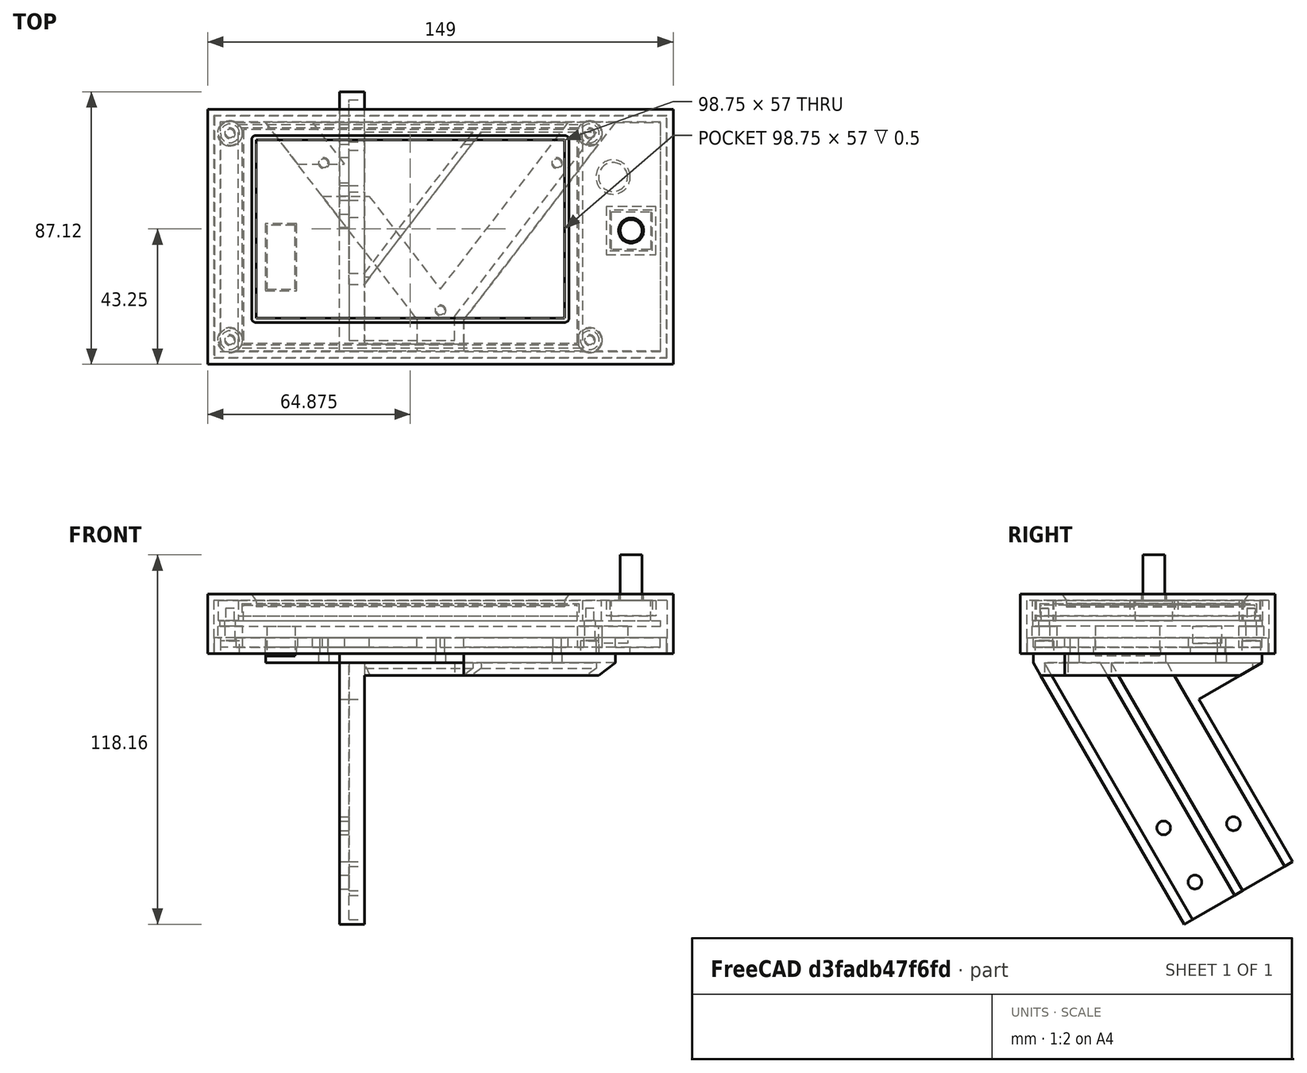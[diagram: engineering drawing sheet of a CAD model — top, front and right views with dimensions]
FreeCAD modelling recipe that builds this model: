
FCSTD DOCUMENT  (FreeCAD 0.20R24840 (Git))
Label: ender 3 v2 dwin case
License: Creative Commons Attribution
LicenseURL: http://creativecommons.org/licenses/by/4.0/
objects: Sketcher::SketchObject×41, PartDesign::Pad×23, PartDesign::Pocket×14, PartDesign::Body×5, PartDesign::SubShapeBinder×5, PartDesign::Groove×4, Part::Feature×2, Part::Mirroring×2, App::Part×1
note: 137 computed .brp shape members not serialized (recipe doc carries the construction recipe); baked Part::Feature solids carry a one-line shape summary decoded from their .brp

FEATURE [Sketcher::SketchObject] Sketch
  FullyConstrained = true
  MapMode = 5
  Support = -> [XY_Plane]
  sketch-geometry (4):
    g0: LineSegment StartX=0 StartY=0 StartZ=0 EndX=141 EndY=0 EndZ=0
    g1: LineSegment StartX=141 StartY=0 StartZ=0 EndX=141 EndY=73.5 EndZ=0
    g2: LineSegment StartX=141 StartY=73.5 StartZ=0 EndX=0 EndY=73.5 EndZ=0
    g3: LineSegment StartX=0 StartY=73.5 StartZ=0 EndX=0 EndY=0 EndZ=0
  constraints (11):
    c: Coincident(g0,g1)
    c: Coincident(g1,g2)
    c: Coincident(g2,g3)
    c: Coincident(g3,g0)
    c: Horizontal(g0)
    c: Horizontal(g2)
    c: Vertical(g1)
    c: Vertical(g3)
    c: Coincident(g0,g-1)
    c: Distance(g2) = 141
    c: Distance(g3) = 73.5
FEATURE [PartDesign::Pad] Pad
  Direction = (0,0,1)
  Length = 1.75
  Length2 = 100
  Profile = -> Sketch
  Type = 0
FEATURE [Sketcher::SketchObject] Sketch001
  FullyConstrained = true
  MapMode = 5
  Placement = pos=(0,0,1.75) rot=(0,0,1;0rad)
  Support = -> [Pad]
  sketch-geometry (4):
    g0: LineSegment StartX=7.5 StartY=2.75 StartZ=0 EndX=114.25 EndY=2.75 EndZ=0
    g1: LineSegment StartX=114.25 StartY=2.75 StartZ=0 EndX=114.25 EndY=71 EndZ=0
    g2: LineSegment StartX=114.25 StartY=71 StartZ=0 EndX=7.5 EndY=71 EndZ=0
    g3: LineSegment StartX=7.5 StartY=71 StartZ=0 EndX=7.5 EndY=2.75 EndZ=0
  constraints (12):
    c: Coincident(g0,g1)
    c: Coincident(g1,g2)
    c: Coincident(g2,g3)
    c: Coincident(g3,g0)
    c: Horizontal(g0)
    c: Horizontal(g2)
    c: Vertical(g1)
    c: Vertical(g3)
    c: Distance(g3) = 68.25
    c: Distance(g2) = 106.75
    c: DistanceX(g-1,g0) = 7.5
    c: DistanceY(g-1,g0) = 2.75
FEATURE [PartDesign::Pad] Pad001
  BaseFeature = -> Pad
  Direction = (0,0,1)
  Length = 5
  Length2 = 100
  Profile = -> Sketch001
  Type = 0
FEATURE [Sketcher::SketchObject] Sketch002
  ExternalGeometry = -> [Pad001]
  FullyConstrained = true
  MapMode = 5
  Placement = pos=(0,0,6.75) rot=(0,0,1;0rad)
  Support = -> [Pad001]
  sketch-geometry (8):
    g0: LineSegment StartX=11.5 StartY=67.75 StartZ=0 EndX=110.25 EndY=67.75 EndZ=0
    g1: LineSegment StartX=110.25 StartY=67.75 StartZ=0 EndX=110.25 EndY=10.75 EndZ=0
    g2: LineSegment StartX=110.25 StartY=10.75 StartZ=0 EndX=11.5 EndY=10.75 EndZ=0
    g3: LineSegment StartX=11.5 StartY=10.75 StartZ=0 EndX=11.5 EndY=67.75 EndZ=0
    g4: LineSegment StartX=110.25 StartY=67.75 StartZ=0 EndX=114.25 EndY=67.75 EndZ=0
    g5: LineSegment StartX=11.5 StartY=67.75 StartZ=0 EndX=7.5 EndY=67.75 EndZ=0
    g6: LineSegment StartX=11.5 StartY=67.75 StartZ=0 EndX=11.5 EndY=71 EndZ=0
    g7: LineSegment StartX=11.5 StartY=10.75 StartZ=0 EndX=11.5 EndY=2.75 EndZ=0
  constraints (24):
    c: Coincident(g0,g1)
    c: Coincident(g1,g2)
    c: Coincident(g2,g3)
    c: Coincident(g3,g0)
    c: Horizontal(g0)
    c: Horizontal(g2)
    c: Vertical(g1)
    c: Vertical(g3)
    c: Coincident(g4,g0)
    c: PointOnObject(g4,g-4)
    c: Coincident(g5,g0)
    c: PointOnObject(g5,g-6)
    c: Coincident(g6,g0)
    c: PointOnObject(g6,g-3)
    c: Vertical(g6)
    c: Coincident(g7,g2)
    c: PointOnObject(g7,g-5)
    c: Vertical(g7)
    c: Horizontal(g5)
    c: Horizontal(g4)
    c: Distance(g5) = 4
    c: Distance(g6) = 3.25
    c: Equal(g5,g4)
    c: Distance(g7) = 8
FEATURE [PartDesign::Pocket] Pocket
  BaseFeature = -> Pad001
  Length = 0.5
  Length2 = 100
  Profile = -> Sketch002
  Type = 0
FEATURE [Sketcher::SketchObject] Sketch003
  ExternalGeometry = -> [Pocket]
  FullyConstrained = true
  MapMode = 5
  Placement = pos=(0,0,1.75) rot=(0,0,1;0rad)
  Support = -> [Pocket]
  sketch-geometry (4):
    g0: LineSegment StartX=125.25 StartY=44.75 StartZ=0 EndX=137.75 EndY=44.75 EndZ=0
    g1: LineSegment StartX=137.75 StartY=44.75 StartZ=0 EndX=137.75 EndY=32.75 EndZ=0
    g2: LineSegment StartX=137.75 StartY=32.75 StartZ=0 EndX=125.25 EndY=32.75 EndZ=0
    g3: LineSegment StartX=125.25 StartY=32.75 StartZ=0 EndX=125.25 EndY=44.75 EndZ=0
  constraints (12):
    c: Coincident(g0,g1)
    c: Coincident(g1,g2)
    c: Coincident(g2,g3)
    c: Coincident(g3,g0)
    c: Horizontal(g0)
    c: Horizontal(g2)
    c: Vertical(g1)
    c: Vertical(g3)
    c: Distance(g0) = 12.5
    c: Distance(g1) = 12
    c: DistanceY(g0,g-3) = 28.75
    c: DistanceX(g0,g-3) = 3.25
FEATURE [PartDesign::Pad] Pad002
  BaseFeature = -> Pocket
  Direction = (0,0,1)
  Length = 6.35
  Length2 = 100
  Profile = -> Sketch003
  Type = 0
FEATURE [Sketcher::SketchObject] Sketch004
  ExternalGeometry = -> [Pad002]
  FullyConstrained = true
  MapMode = 5
  Placement = pos=(0,0,8.1) rot=(0,0,1;0rad)
  Support = -> [Pad002]
  sketch-geometry (5):
    g0: Circle CenterX=131.5 CenterY=38.75 CenterZ=0 NormalX=0 NormalY=0 NormalZ=1 AngleXU=0 Radius=3.5
    g1: LineSegment StartX=131.5 StartY=38.75 StartZ=0 EndX=131.5 EndY=44.75 EndZ=0
    g2: LineSegment StartX=131.5 StartY=38.75 StartZ=0 EndX=131.5 EndY=32.75 EndZ=0
    g3: LineSegment StartX=131.5 StartY=38.75 StartZ=0 EndX=137.75 EndY=38.75 EndZ=0
    g4: LineSegment StartX=131.5 StartY=38.75 StartZ=0 EndX=125.25 EndY=38.75 EndZ=0
  constraints (15):
    c: Radius(g0) = 3.5
    c: Coincident(g1,g0)
    c: PointOnObject(g1,g-3)
    c: Vertical(g1)
    c: Coincident(g2,g0)
    c: PointOnObject(g2,g-4)
    c: Vertical(g2)
    c: Coincident(g3,g0)
    c: PointOnObject(g3,g-6)
    c: Horizontal(g3)
    c: Coincident(g4,g0)
    c: PointOnObject(g4,g-5)
    c: Horizontal(g4)
    c: Equal(g3,g4)
    c: Equal(g1,g2)
FEATURE [PartDesign::Pad] Pad003
  BaseFeature = -> Pad002
  Direction = (0,0,1)
  Length = 14.75
  Length2 = 100
  Profile = -> Sketch004
  Type = 0
FEATURE [Sketcher::SketchObject] Sketch005
  ExternalGeometry = -> [Pad003]
  FullyConstrained = true
  MapMode = 5
  Placement = pos=(0,0,0) rot=(1,0,0;3.14159rad)
  Support = -> [Pad003]
  sketch-geometry (5):
    g0: Circle CenterX=125.725 CenterY=-55.875 CenterZ=0 NormalX=0 NormalY=0 NormalZ=1 AngleXU=0 Radius=4.625
    g1: LineSegment StartX=130.35 StartY=-55.875 StartZ=0 EndX=141 EndY=-55.875 EndZ=0
    g2: LineSegment StartX=130.35 StartY=-55.875 StartZ=0 EndX=125.725 EndY=-55.875 EndZ=0
    g3: LineSegment StartX=125.725 StartY=-60.5 StartZ=0 EndX=125.725 EndY=-73.5 EndZ=0
    g4: LineSegment StartX=125.725 StartY=-60.5 StartZ=0 EndX=125.725 EndY=-55.875 EndZ=0
  constraints (15):
    c: Radius(g0) = 4.625
    c: PointOnObject(g1,g0)
    c: PointOnObject(g1,g-3)
    c: Horizontal(g1)
    c: Distance(g1) = 10.65
    c: Coincident(g2,g1)
    c: Coincident(g2,g0)
    c: Horizontal(g2)
    c: PointOnObject(g3,g0)
    c: PointOnObject(g3,g-4)
    c: Vertical(g3)
    c: Coincident(g4,g3)
    c: Coincident(g4,g0)
    c: Vertical(g4)
    c: Distance(g3) = 13
FEATURE [PartDesign::Pad] Pad004
  BaseFeature = -> Pad003
  Direction = (0,0,-1)
  Length = 5.5
  Length2 = 100
  Profile = -> Sketch005
  Type = 0
FEATURE [Sketcher::SketchObject] Sketch006
  FullyConstrained = true
  MapMode = 5
  Placement = pos=(0,0,0) rot=(1,0,0;3.14159rad)
  Support = -> [Pad004]
  sketch-geometry (4):
    g0: LineSegment StartX=15 StartY=-20 StartZ=0 EndX=24 EndY=-20 EndZ=0
    g1: LineSegment StartX=24 StartY=-20 StartZ=0 EndX=24 EndY=-40.5 EndZ=0
    g2: LineSegment StartX=24 StartY=-40.5 StartZ=0 EndX=15 EndY=-40.5 EndZ=0
    g3: LineSegment StartX=15 StartY=-40.5 StartZ=0 EndX=15 EndY=-20 EndZ=0
  constraints (12):
    c: Coincident(g0,g1)
    c: Coincident(g1,g2)
    c: Coincident(g2,g3)
    c: Coincident(g3,g0)
    c: Horizontal(g0)
    c: Horizontal(g2)
    c: Vertical(g1)
    c: Vertical(g3)
    c: Distance(g2) = 9
    c: Distance(g3) = 20.5
    c: DistanceY(g0,g-1) = 20
    c: DistanceX(g-1,g0) = 15
FEATURE [PartDesign::Pad] Pad005
  BaseFeature = -> Pad004
  Direction = (0,0,-1)
  Length = 9.5
  Length2 = 100
  Profile = -> Sketch006
  Type = 0
FEATURE [Sketcher::SketchObject] Sketch007
  ExternalGeometry = -> [Pad005]
  FullyConstrained = true
  MapMode = 5
  Placement = pos=(0,0,1.75) rot=(0,0,1;0rad)
  Support = -> [Pad005]
  sketch-geometry (19):
    g0: Circle CenterX=3.1665 CenterY=3.6665 CenterZ=0 NormalX=0 NormalY=0 NormalZ=1 AngleXU=0 Radius=1.6665
    g1: Circle CenterX=3.1665 CenterY=69.8335 CenterZ=0 NormalX=0 NormalY=0 NormalZ=1 AngleXU=0 Radius=1.6665
    g2: LineSegment StartX=3.1665 StartY=71.5 StartZ=0 EndX=3.1665 EndY=73.5 EndZ=0
    g3: LineSegment StartX=3.1665 StartY=69.8335 StartZ=0 EndX=3.1665 EndY=71.5 EndZ=0
    g4: LineSegment StartX=3.1665 StartY=69.8335 StartZ=0 EndX=1.5 EndY=69.8335 EndZ=0
    g5: LineSegment StartX=1.5 StartY=69.8335 StartZ=0 EndX=0 EndY=69.8335 EndZ=0
    g6: LineSegment StartX=3.1665 StartY=3.6665 StartZ=0 EndX=3.1665 EndY=2 EndZ=0
    g7: LineSegment StartX=3.1665 StartY=3.6665 StartZ=0 EndX=1.5 EndY=3.6665 EndZ=0
    g8: LineSegment StartX=1.5 StartY=3.6665 StartZ=0 EndX=0 EndY=3.6665 EndZ=0
    g9: LineSegment StartX=3.1665 StartY=2 StartZ=0 EndX=3.1665 EndY=0 EndZ=0
    g10: Circle CenterX=118.284 CenterY=3.6665 CenterZ=0 NormalX=0 NormalY=0 NormalZ=1 AngleXU=0 Radius=1.6665
    g11: Circle CenterX=118.284 CenterY=69.8335 CenterZ=0 NormalX=0 NormalY=0 NormalZ=1 AngleXU=0 Radius=1.6665
    g12: LineSegment StartX=118.284 StartY=3.6665 StartZ=0 EndX=118.284 EndY=2 EndZ=0
    g13: LineSegment StartX=118.284 StartY=2 StartZ=0 EndX=118.284 EndY=0 EndZ=0
    g14: LineSegment StartX=118.284 StartY=69.8335 StartZ=0 EndX=118.284 EndY=71.5 EndZ=0
    g15: LineSegment StartX=118.284 StartY=71.5 StartZ=0 EndX=118.284 EndY=73.5 EndZ=0
    g16: LineSegment StartX=118.284 StartY=69.8335 StartZ=0 EndX=118.284 EndY=3.6665 EndZ=0
    g17: LineSegment StartX=141 StartY=3.6665 StartZ=0 EndX=119.95 EndY=3.6665 EndZ=0
    g18: LineSegment StartX=119.95 StartY=3.6665 StartZ=0 EndX=118.284 EndY=3.6665 EndZ=0
  constraints (56):
    c: Radius(g0) = 1.6665
    c: Equal(g1,g0)
    c: PointOnObject(g2,g1)
    c: PointOnObject(g2,g-6)
    c: Vertical(g2)
    c: Coincident(g3,g1)
    c: Coincident(g3,g2)
    c: Vertical(g3)
    c: Coincident(g4,g1)
    c: PointOnObject(g4,g1)
    c: Horizontal(g4)
    c: Coincident(g5,g4)
    c: PointOnObject(g5,g-4)
    c: Horizontal(g5)
    c: Distance(g2) = 2
    c: Distance(g5) = 1.5
    c: Coincident(g6,g0)
    c: PointOnObject(g6,g0)
    c: Vertical(g6)
    c: Coincident(g7,g0)
    c: PointOnObject(g7,g0)
    c: Horizontal(g7)
    c: Coincident(g8,g7)
    c: PointOnObject(g8,g-4)
    c: Horizontal(g8)
    c: Coincident(g9,g6)
    c: PointOnObject(g9,g-3)
    c: Vertical(g9)
    c: Distance(g8) = 1.5
    c: Distance(g9) = 2
    c: Equal(g10,g11)
    c: Equal(g11,g1)
    c: Coincident(g12,g10)
    c: PointOnObject(g12,g10)
    c: Vertical(g12)
    c: Coincident(g13,g12)
    c: PointOnObject(g13,g-3)
    c: Vertical(g13)
    c: Distance(g13) = 2
    c: Coincident(g14,g11)
    c: PointOnObject(g14,g11)
    c: Vertical(g14)
    c: Coincident(g15,g14)
    c: PointOnObject(g15,g-6)
    c: Vertical(g15)
    c: Distance(g15) = 2
    c: Coincident(g16,g11)
    c: Coincident(g16,g10)
    c: Vertical(g16)
    c: PointOnObject(g17,g-5)
    c: PointOnObject(g17,g10)
    c: Horizontal(g17)
    c: Coincident(g18,g17)
    c: Coincident(g18,g10)
    c: Horizontal(g18)
    c: Distance(g17) = 21.05
FEATURE [PartDesign::Pocket] Pocket001
  BaseFeature = -> Pad005
  Length = 5
  Length2 = 100
  Profile = -> Sketch007
  Type = 1
FEATURE [PartDesign::Body] Body  label="T5UIC1"
  Group = -> [Sketch,Pad,Sketch001,Pad001,Sketch002,Pocket,Sketch003,Pad002,Sketch004,Pad003,Sketch005,Pad004,Sketch006,Pad005,Sketch007,Pocket001]
  Origin = -> Origin
  Tip = -> Pocket001
FEATURE [PartDesign::SubShapeBinder] Binder
  BindMode = 0
  ClaimChildren = false
  Context = -> Body001 [Binder.]
  Fuse = false
  MakeFace = true
  PartialLoad = false
  Relative = true
  Support = -> [Body]
  _Version = 2
FEATURE [Sketcher::SketchObject] Sketch008
  AttachmentOffset = pos=(0,0,0.2) rot=(0,0,1;0rad)
  ExternalGeometry = -> [Binder]
  FullyConstrained = true
  MapMode = 5
  Placement = pos=(0,0,8.3) rot=(0,0,1;0rad)
  Support = -> [Binder]
  sketch-geometry (9):
    g0: LineSegment StartX=-4 StartY=77.5 StartZ=0 EndX=145 EndY=77.5 EndZ=0
    g1: LineSegment StartX=145 StartY=77.5 StartZ=0 EndX=145 EndY=-4 EndZ=0
    g2: LineSegment StartX=145 StartY=-4 StartZ=0 EndX=-4 EndY=-4 EndZ=0
    g3: LineSegment StartX=-4 StartY=-4 StartZ=0 EndX=-4 EndY=77.5 EndZ=0
    g4: LineSegment StartX=11.5 StartY=67.75 StartZ=0 EndX=110.25 EndY=67.75 EndZ=0
    g5: LineSegment StartX=110.25 StartY=67.75 StartZ=0 EndX=110.25 EndY=10.75 EndZ=0
    g6: LineSegment StartX=110.25 StartY=10.75 StartZ=0 EndX=11.5 EndY=10.75 EndZ=0
    g7: LineSegment StartX=11.5 StartY=10.75 StartZ=0 EndX=11.5 EndY=67.75 EndZ=0
    g8: Circle CenterX=131.5 CenterY=38.75 CenterZ=0 NormalX=0 NormalY=0 NormalZ=1 AngleXU=0 Radius=4
  constraints (24):
    c: Coincident(g0,g1)
    c: Coincident(g1,g2)
    c: Coincident(g2,g3)
    c: Coincident(g3,g0)
    c: Horizontal(g0)
    c: Horizontal(g2)
    c: Vertical(g1)
    c: Vertical(g3)
    c: Coincident(g4,g5)
    c: Coincident(g5,g6)
    c: Coincident(g6,g7)
    c: Coincident(g7,g4)
    c: Horizontal(g4)
    c: Horizontal(g6)
    c: Vertical(g5)
    c: Vertical(g7)
    c: Coincident(g4,g-6)
    c: Coincident(g5,g-5)
    c: Coincident(g8,g-11)
    c: Radius(g8) = 4
    c: DistanceX(g-9,g1) = 4
    c: DistanceY(g1,g-9) = 4
    c: DistanceY(g-10,g0) = 4
    c: DistanceX(g0,g-10) = 4
FEATURE [PartDesign::Pad] Pad006
  Direction = (0,0,1)
  Length = 2
  Length2 = 100
  Profile = -> Sketch008
  Type = 0
FEATURE [Sketcher::SketchObject] Sketch009
  ExternalGeometry = -> [Binder]
  FullyConstrained = true
  MapMode = 5
  Placement = pos=(0,0,8.3) rot=(1,0,0;3.14159rad)
  Support = -> [Pad006]
  sketch-geometry (16):
    g0: LineSegment StartX=124.75 StartY=-32.25 StartZ=0 EndX=138.25 EndY=-32.25 EndZ=0
    g1: LineSegment StartX=138.25 StartY=-32.25 StartZ=0 EndX=138.25 EndY=-45.25 EndZ=0
    g2: LineSegment StartX=138.25 StartY=-45.25 StartZ=0 EndX=124.75 EndY=-45.25 EndZ=0
    g3: LineSegment StartX=124.75 StartY=-45.25 StartZ=0 EndX=124.75 EndY=-32.25 EndZ=0
    g4: LineSegment StartX=123.55 StartY=-31.05 StartZ=0 EndX=139.45 EndY=-31.05 EndZ=0
    g5: LineSegment StartX=139.45 StartY=-31.05 StartZ=0 EndX=139.45 EndY=-46.45 EndZ=0
    g6: LineSegment StartX=139.45 StartY=-46.45 StartZ=0 EndX=123.55 EndY=-46.45 EndZ=0
    g7: LineSegment StartX=123.55 StartY=-46.45 StartZ=0 EndX=123.55 EndY=-31.05 EndZ=0
    g8: LineSegment StartX=7 StartY=-2.25 StartZ=0 EndX=114.75 EndY=-2.25 EndZ=0
    g9: LineSegment StartX=114.75 StartY=-2.25 StartZ=0 EndX=114.75 EndY=-71.5 EndZ=0
    g10: LineSegment StartX=114.75 StartY=-71.5 StartZ=0 EndX=7 EndY=-71.5 EndZ=0
    g11: LineSegment StartX=7 StartY=-71.5 StartZ=0 EndX=7 EndY=-2.25 EndZ=0
    g12: LineSegment StartX=5.8 StartY=-72.7 StartZ=0 EndX=115.95 EndY=-72.7 EndZ=0
    g13: LineSegment StartX=115.95 StartY=-72.7 StartZ=0 EndX=115.95 EndY=-1.05 EndZ=0
    g14: LineSegment StartX=115.95 StartY=-1.05 StartZ=0 EndX=5.8 EndY=-1.05 EndZ=0
    g15: LineSegment StartX=5.8 StartY=-1.05 StartZ=0 EndX=5.8 EndY=-72.7 EndZ=0
  constraints (48):
    c: Coincident(g0,g1)
    c: Coincident(g1,g2)
    c: Coincident(g2,g3)
    c: Coincident(g3,g0)
    c: Horizontal(g0)
    c: Horizontal(g2)
    c: Vertical(g1)
    c: Vertical(g3)
    c: DistanceY(g-3,g0) = 0.5
    c: DistanceX(g-3,g0) = 0.5
    c: DistanceY(g2,g-4) = 0.5
    c: DistanceX(g2,g-4) = 0.5
    c: Coincident(g4,g5)
    c: Coincident(g5,g6)
    c: Coincident(g6,g7)
    c: Coincident(g7,g4)
    c: Horizontal(g4)
    c: Horizontal(g6)
    c: Vertical(g5)
    c: Vertical(g7)
    c: DistanceY(g0,g4) = 1.2
    c: DistanceX(g4,g0) = 1.2
    c: DistanceX(g1,g5) = 1.2
    c: DistanceY(g5,g1) = 1.2
    c: Coincident(g8,g9)
    c: Coincident(g9,g10)
    c: Coincident(g10,g11)
    c: Coincident(g11,g8)
    c: Horizontal(g8)
    c: Horizontal(g10)
    c: Vertical(g9)
    c: Vertical(g11)
    c: DistanceX(g-7,g9) = 0.5
    c: DistanceY(g9,g-7) = 0.5
    c: DistanceX(g8,g-8) = 0.5
    c: DistanceY(g-8,g8) = 0.5
    c: Coincident(g12,g13)
    c: Coincident(g13,g14)
    c: Coincident(g14,g15)
    c: Coincident(g15,g12)
    c: Horizontal(g12)
    c: Horizontal(g14)
    c: Vertical(g13)
    c: Vertical(g15)
    c: DistanceX(g8,g13) = 1.2
    c: DistanceY(g8,g13) = 1.2
    c: DistanceX(g12,g10) = 1.2
    c: DistanceY(g12,g10) = 1.2
FEATURE [PartDesign::Pad] Pad007
  BaseFeature = -> Pad006
  Direction = (0,0,-1)
  Length = 5
  Length2 = 100
  Profile = -> Sketch009
  Type = 0
FEATURE [Sketcher::SketchObject] Sketch010
  ExternalGeometry = -> [Pad007]
  FullyConstrained = true
  MapMode = 5
  Placement = pos=(0,0,8.3) rot=(1,0,0;3.14159rad)
  Support = -> [Pad007]
  sketch-geometry (8):
    g0: LineSegment StartX=11.5 StartY=-10.75 StartZ=0 EndX=110.25 EndY=-10.75 EndZ=0
    g1: LineSegment StartX=110.25 StartY=-10.75 StartZ=0 EndX=110.25 EndY=-67.75 EndZ=0
    g2: LineSegment StartX=110.25 StartY=-67.75 StartZ=0 EndX=11.5 EndY=-67.75 EndZ=0
    g3: LineSegment StartX=11.5 StartY=-67.75 StartZ=0 EndX=11.5 EndY=-10.75 EndZ=0
    g4: LineSegment StartX=7 StartY=-2.25 StartZ=0 EndX=114.75 EndY=-2.25 EndZ=0
    g5: LineSegment StartX=114.75 StartY=-2.25 StartZ=0 EndX=114.75 EndY=-71.5 EndZ=0
    g6: LineSegment StartX=114.75 StartY=-71.5 StartZ=0 EndX=7 EndY=-71.5 EndZ=0
    g7: LineSegment StartX=7 StartY=-71.5 StartZ=0 EndX=7 EndY=-2.25 EndZ=0
  constraints (20):
    c: Coincident(g0,g1)
    c: Coincident(g1,g2)
    c: Coincident(g2,g3)
    c: Coincident(g3,g0)
    c: Horizontal(g0)
    c: Horizontal(g2)
    c: Vertical(g1)
    c: Vertical(g3)
    c: Coincident(g0,g-4)
    c: Coincident(g1,g-3)
    c: Coincident(g4,g5)
    c: Coincident(g5,g6)
    c: Coincident(g6,g7)
    c: Coincident(g7,g4)
    c: Horizontal(g4)
    c: Horizontal(g6)
    c: Vertical(g5)
    c: Vertical(g7)
    c: Coincident(g4,g-6)
    c: Coincident(g5,g-5)
FEATURE [PartDesign::Pad] Pad008
  BaseFeature = -> Pad007
  Direction = (0,0,-1)
  Length = 1
  Length2 = 100
  Profile = -> Sketch010
  Type = 0
FEATURE [Sketcher::SketchObject] Sketch011
  ExternalGeometry = -> [Binder,Pad008]
  FullyConstrained = true
  MapMode = 5
  Placement = pos=(0,0,8.3) rot=(1,0,0;3.14159rad)
  Support = -> [Pad008]
  sketch-geometry (8):
    g0: ArcOfCircle CenterX=3.1665 CenterY=-3.6665 CenterZ=0 NormalX=0 NormalY=0 NormalZ=1 AngleXU=0 Radius=3.75 StartAngle=0.79222 EndAngle=5.49097
    g1: LineSegment StartX=5.8 StartY=-0.996823 StartZ=0 EndX=5.8 EndY=-6.33618 EndZ=0
    g2: ArcOfCircle CenterX=3.1665 CenterY=-69.8335 CenterZ=0 NormalX=0 NormalY=0 NormalZ=1 AngleXU=0 Radius=3.75 StartAngle=0.79222 EndAngle=5.49097
    g3: LineSegment StartX=5.8 StartY=-67.1638 StartZ=0 EndX=5.8 EndY=-72.5032 EndZ=0
    g4: ArcOfCircle CenterX=118.284 CenterY=-69.8335 CenterZ=0 NormalX=0 NormalY=0 NormalZ=1 AngleXU=0 Radius=3.75 StartAngle=4.04075 EndAngle=8.52562
    g5: LineSegment StartX=115.95 StartY=-72.769 StartZ=0 EndX=115.95 EndY=-66.898 EndZ=0
    g6: ArcOfCircle CenterX=118.284 CenterY=-3.6665 CenterZ=0 NormalX=0 NormalY=0 NormalZ=1 AngleXU=0 Radius=3.75 StartAngle=4.04075 EndAngle=8.52562
    g7: LineSegment StartX=115.95 StartY=-0.73098 StartZ=0 EndX=115.95 EndY=-6.60202 EndZ=0
  constraints (24):
    c: PointOnObject(g0,g-7)
    c: PointOnObject(g0,g-7)
    c: Coincident(g0,g-6)
    c: Coincident(g1,g0)
    c: Coincident(g1,g0)
    c: Coincident(g2,g-5)
    c: PointOnObject(g2,g-7)
    c: PointOnObject(g2,g-7)
    c: Equal(g2,g0)
    c: Coincident(g3,g2)
    c: Coincident(g3,g2)
    c: Coincident(g4,g-4)
    c: PointOnObject(g4,g-9)
    c: PointOnObject(g4,g-9)
    c: Equal(g4,g2)
    c: Coincident(g5,g4)
    c: Coincident(g5,g4)
    c: Coincident(g6,g-3)
    c: PointOnObject(g6,g-9)
    c: PointOnObject(g6,g-9)
    c: Radius(g6) = 3.75
    c: Coincident(g7,g6)
    c: Coincident(g7,g6)
    c: Equal(g0,g6)
FEATURE [PartDesign::Pad] Pad009
  BaseFeature = -> Pad008
  Direction = (0,0,-1)
  Length = 10
  Length2 = 100
  Profile = -> Sketch011
  Type = 3
  UpToFace = -> Binder [Face5]
FEATURE [Sketcher::SketchObject] Sketch012
  ExternalGeometry = -> [Pad009]
  FullyConstrained = true
  MapMode = 5
  Placement = pos=(0,0,1.75) rot=(1,0,0;3.14159rad)
  Support = -> [Pad009]
  sketch-geometry (4):
    g0: Circle CenterX=118.284 CenterY=-3.6665 CenterZ=0 NormalX=0 NormalY=0 NormalZ=1 AngleXU=0 Radius=1.375
    g1: Circle CenterX=118.284 CenterY=-69.8335 CenterZ=0 NormalX=0 NormalY=0 NormalZ=1 AngleXU=0 Radius=1.375
    g2: Circle CenterX=3.1665 CenterY=-69.8335 CenterZ=0 NormalX=0 NormalY=0 NormalZ=1 AngleXU=0 Radius=1.375
    g3: Circle CenterX=3.1665 CenterY=-3.6665 CenterZ=0 NormalX=0 NormalY=0 NormalZ=1 AngleXU=0 Radius=1.375
  constraints (8):
    c: Coincident(g0,g-6)
    c: Coincident(g1,g-3)
    c: Coincident(g2,g-4)
    c: Coincident(g3,g-5)
    c: Equal(g3,g2)
    c: Equal(g2,g1)
    c: Equal(g1,g0)
    c: Radius(g0) = 1.375
FEATURE [PartDesign::Pocket] Pocket002
  BaseFeature = -> Pad009
  Length = 4
  Length2 = 100
  Profile = -> Sketch012
  Type = 0
FEATURE [Sketcher::SketchObject] Sketch014
  ExternalGeometry = -> [Pocket002]
  FullyConstrained = true
  MapMode = 5
  Placement = pos=(0,0,8.3) rot=(1,0,0;3.14159rad)
  Support = -> [Pocket002]
  sketch-geometry (8):
    g0: LineSegment StartX=-4 StartY=4 StartZ=0 EndX=145 EndY=4 EndZ=0
    g1: LineSegment StartX=145 StartY=4 StartZ=0 EndX=145 EndY=-77.5 EndZ=0
    g2: LineSegment StartX=145 StartY=-77.5 StartZ=0 EndX=-4 EndY=-77.5 EndZ=0
    g3: LineSegment StartX=-4 StartY=-77.5 StartZ=0 EndX=-4 EndY=4 EndZ=0
    g4: LineSegment StartX=-2 StartY=2 StartZ=0 EndX=143 EndY=2 EndZ=0
    g5: LineSegment StartX=143 StartY=2 StartZ=0 EndX=143 EndY=-75.5 EndZ=0
    g6: LineSegment StartX=143 StartY=-75.5 StartZ=0 EndX=-2 EndY=-75.5 EndZ=0
    g7: LineSegment StartX=-2 StartY=-75.5 StartZ=0 EndX=-2 EndY=2 EndZ=0
  constraints (22):
    c: Coincident(g0,g1)
    c: Coincident(g1,g2)
    c: Coincident(g2,g3)
    c: Coincident(g3,g0)
    c: Horizontal(g0)
    c: Horizontal(g2)
    c: Vertical(g1)
    c: Vertical(g3)
    c: Coincident(g0,g-4)
    c: Coincident(g1,g-3)
    c: Coincident(g4,g5)
    c: Coincident(g5,g6)
    c: Coincident(g6,g7)
    c: Coincident(g7,g4)
    c: Horizontal(g4)
    c: Horizontal(g6)
    c: Vertical(g5)
    c: Vertical(g7)
    c: DistanceX(g5,g1) = 2
    c: DistanceY(g1,g5) = 2
    c: DistanceY(g4,g0) = 2
    c: DistanceX(g0,g4) = 2
FEATURE [PartDesign::Pad] Pad011
  BaseFeature = -> Pocket002
  Direction = (0,0,-1)
  Length = 17
  Length2 = 100
  Profile = -> Sketch014
  Type = 0
FEATURE [Sketcher::SketchObject] Sketch015
  ExternalGeometry = -> [Pad011]
  FullyConstrained = true
  MapMode = 5
  Placement = pos=(11.5,0,0) rot=(0.57735,0.57735,0.57735;2.0944rad)
  Support = -> [Pad011]
  sketch-geometry (6):
    g0: LineSegment StartX=67.75 StartY=8.3 StartZ=0 EndX=67.75 EndY=10.3 EndZ=0
    g1: LineSegment StartX=67.75 StartY=8.3 StartZ=0 EndX=69.1504 EndY=10.3 EndZ=0
    g2: LineSegment StartX=69.1504 StartY=10.3 StartZ=0 EndX=67.75 EndY=10.3 EndZ=0
    g3: LineSegment StartX=10.75 StartY=8.3 StartZ=0 EndX=10.75 EndY=10.3 EndZ=0
    g4: LineSegment StartX=10.75 StartY=10.3 StartZ=0 EndX=9.34958 EndY=10.3 EndZ=0
    g5: LineSegment StartX=9.34958 StartY=10.3 StartZ=0 EndX=10.75 EndY=8.3 EndZ=0
  constraints (14):
    c: Coincident(g0,g-5)
    c: Coincident(g0,g-5)
    c: Coincident(g1,g0)
    c: PointOnObject(g1,g-4)
    c: Coincident(g2,g1)
    c: Coincident(g2,g0)
    c: Angle(g2,g1) = 0.959931
    c: Coincident(g3,g-3)
    c: Coincident(g3,g-3)
    c: Coincident(g4,g3)
    c: PointOnObject(g4,g-4)
    c: Coincident(g5,g4)
    c: Coincident(g5,g3)
    c: Equal(g4,g2)
FEATURE [PartDesign::Pocket] Pocket003
  BaseFeature = -> Pad011
  Length = 0
  Length2 = 100
  Profile = -> Sketch015
  Reversed = true
  Type = 3
  UpToFace = -> Pad011 [Face12]
FEATURE [Sketcher::SketchObject] Sketch016
  ExternalGeometry = -> [Pocket003]
  FullyConstrained = true
  MapMode = 5
  Placement = pos=(0,10.75,0) rot=(0,0.707107,0.707107;3.14159rad)
  Support = -> [Pocket003]
  sketch-geometry (6):
    g0: LineSegment StartX=-110.25 StartY=8.3 StartZ=0 EndX=-110.25 EndY=10.3 EndZ=0
    g1: LineSegment StartX=-110.25 StartY=10.3 StartZ=0 EndX=-111.65 EndY=10.3 EndZ=0
    g2: LineSegment StartX=-111.65 StartY=10.3 StartZ=0 EndX=-110.25 EndY=8.3 EndZ=0
    g3: LineSegment StartX=-11.5 StartY=8.3 StartZ=0 EndX=-10.0996 EndY=10.3 EndZ=0
    g4: LineSegment StartX=-11.5 StartY=8.3 StartZ=0 EndX=-11.5 EndY=10.3 EndZ=0
    g5: LineSegment StartX=-11.5 StartY=10.3 StartZ=0 EndX=-10.0996 EndY=10.3 EndZ=0
  constraints (16):
    c: Coincident(g0,g-5)
    c: PointOnObject(g0,g-3)
    c: Coincident(g1,g0)
    c: PointOnObject(g1,g-3)
    c: Coincident(g2,g1)
    c: Coincident(g2,g0)
    c: Vertical(g0)
    c: Angle(g2,g1) = 0.959931
    c: Coincident(g3,g-4)
    c: PointOnObject(g3,g-3)
    c: Coincident(g4,g3)
    c: PointOnObject(g4,g-3)
    c: Vertical(g4)
    c: Coincident(g5,g4)
    c: Coincident(g5,g3)
    c: Equal(g5,g1)
FEATURE [PartDesign::Pocket] Pocket004
  BaseFeature = -> Pocket003
  Length = 0
  Length2 = 100
  Profile = -> Sketch016
  Reversed = true
  Type = 3
  UpToFace = -> Pocket003 [Face26]
FEATURE [Sketcher::SketchObject] Sketch017
  ExternalGeometry = -> [Pocket004]
  FullyConstrained = true
  MapMode = 5
  Placement = pos=(0,10.75,0) rot=(0,0.707107,0.707107;3.14159rad)
  Support = -> [Pocket004]
  sketch-geometry (3):
    g0: LineSegment StartX=-110.25 StartY=10.3 StartZ=0 EndX=-111.65 EndY=10.3 EndZ=0
    g1: LineSegment StartX=-111.65 StartY=10.3 StartZ=0 EndX=-110.25 EndY=8.3 EndZ=0
    g2: LineSegment StartX=-110.25 StartY=8.3 StartZ=0 EndX=-110.25 EndY=10.3 EndZ=0
  constraints (6):
    c: Coincident(g0,g-4)
    c: Coincident(g0,g-3)
    c: Coincident(g1,g0)
    c: Coincident(g1,g-4)
    c: Coincident(g2,g1)
    c: Coincident(g2,g0)
FEATURE [PartDesign::Groove] Groove
  Angle = 360
  Axis = (0,0,1)
  Base = (110.25,10.75,8.3)
  BaseFeature = -> Pocket004
  Profile = -> Sketch017
  ReferenceAxis = -> Pocket004 [Edge52]
FEATURE [Sketcher::SketchObject] Sketch018
  ExternalGeometry = -> [Groove]
  FullyConstrained = true
  MapMode = 5
  Placement = pos=(0,67.75,0) rot=(1,0,0;1.5708rad)
  Support = -> [Groove]
  sketch-geometry (3):
    g0: LineSegment StartX=111.65 StartY=10.3 StartZ=0 EndX=110.25 EndY=10.3 EndZ=0
    g1: LineSegment StartX=110.25 StartY=10.3 StartZ=0 EndX=110.25 EndY=8.3 EndZ=0
    g2: LineSegment StartX=110.25 StartY=8.3 StartZ=0 EndX=111.65 EndY=10.3 EndZ=0
  constraints (6):
    c: Coincident(g0,g-3)
    c: Coincident(g0,g-4)
    c: Coincident(g1,g0)
    c: Coincident(g1,g-4)
    c: Coincident(g2,g1)
    c: Coincident(g2,g0)
FEATURE [PartDesign::Groove] Groove001
  Angle = 360
  Axis = (0,0,1)
  Base = (110.25,67.75,8.3)
  BaseFeature = -> Groove
  Profile = -> Sketch018
  ReferenceAxis = -> Groove [Edge47]
FEATURE [Sketcher::SketchObject] Sketch019
  ExternalGeometry = -> [Groove001]
  FullyConstrained = true
  MapMode = 5
  Placement = pos=(11.5,0,0) rot=(0.57735,0.57735,0.57735;2.0944rad)
  Support = -> [Groove001]
  sketch-geometry (3):
    g0: LineSegment StartX=67.75 StartY=8.3 StartZ=0 EndX=69.1504 EndY=10.3 EndZ=0
    g1: LineSegment StartX=69.1504 StartY=10.3 StartZ=0 EndX=67.75 EndY=10.3 EndZ=0
    g2: LineSegment StartX=67.75 StartY=10.3 StartZ=0 EndX=67.75 EndY=8.3 EndZ=0
  constraints (6):
    c: Coincident(g0,g-4)
    c: Coincident(g0,g-3)
    c: Coincident(g1,g0)
    c: Coincident(g1,g-4)
    c: Coincident(g2,g1)
    c: Coincident(g2,g0)
FEATURE [PartDesign::Groove] Groove002
  Angle = 360
  Axis = (0,0,1)
  Base = (11.5,67.75,8.3)
  BaseFeature = -> Groove001
  Profile = -> Sketch019
  ReferenceAxis = -> Groove001 [Edge42]
FEATURE [Sketcher::SketchObject] Sketch020
  ExternalGeometry = -> [Groove002]
  FullyConstrained = true
  MapMode = 5
  Placement = pos=(0,10.75,0) rot=(0,0.707107,0.707107;3.14159rad)
  Support = -> [Groove002]
  sketch-geometry (3):
    g0: LineSegment StartX=-11.5 StartY=8.3 StartZ=0 EndX=-10.0996 EndY=10.3 EndZ=0
    g1: LineSegment StartX=-11.5 StartY=10.3 StartZ=0 EndX=-11.5 EndY=8.3 EndZ=0
    g2: LineSegment StartX=-10.0996 StartY=10.3 StartZ=0 EndX=-11.5 EndY=10.3 EndZ=0
  constraints (6):
    c: Coincident(g0,g-4)
    c: Coincident(g0,g-4)
    c: Coincident(g1,g-3)
    c: Coincident(g1,g0)
    c: Coincident(g2,g0)
    c: Coincident(g2,g1)
FEATURE [PartDesign::Groove] Groove003
  Angle = 360
  Axis = (0,0,1)
  Base = (11.5,10.75,8.3)
  BaseFeature = -> Groove002
  Profile = -> Sketch020
  ReferenceAxis = -> Groove002 [Edge38]
  Reversed = true
FEATURE [PartDesign::Body] Body001  label="Front"
  Group = -> [Binder,Sketch008,Pad006,Sketch009,Pad007,Sketch010,Pad008,Sketch011,Pad009,Sketch012,Pocket002,Sketch014,Pad011,Sketch015,Pocket003,Sketch016,Pocket004,Sketch017,Groove,Sketch018,Groove001,Sketch019,Groove002,Sketch020,Groove003]
  Origin = -> Origin001
  Tip = -> Groove003
FEATURE [PartDesign::SubShapeBinder] Binder001
  BindMode = 0
  ClaimChildren = false
  Context = -> Part [Body002.Binder001.]
  Fuse = false
  MakeFace = true
  PartialLoad = false
  Relative = true
  Support = -> [Body001]
  _Version = 2
FEATURE [PartDesign::SubShapeBinder] Binder002
  BindMode = 0
  ClaimChildren = false
  Context = -> Part [Body002.Binder002.]
  Fuse = false
  MakeFace = true
  PartialLoad = false
  Relative = true
  Support = -> [Body]
  _Version = 2
FEATURE [Sketcher::SketchObject] Sketch021
  ExternalGeometry = -> [Binder001,Binder002]
  FullyConstrained = true
  MapMode = 5
  Placement = pos=(0,0,-8.7) rot=(1,0,0;3.14159rad)
  Support = -> [Binder001]
  sketch-geometry (13):
    g0: LineSegment StartX=-1.8 StartY=1.8 StartZ=0 EndX=142.8 EndY=1.8 EndZ=0
    g1: LineSegment StartX=142.8 StartY=1.8 StartZ=0 EndX=142.8 EndY=-75.3 EndZ=0
    g2: LineSegment StartX=142.8 StartY=-75.3 StartZ=0 EndX=-1.8 EndY=-75.3 EndZ=0
    g3: LineSegment StartX=-1.8 StartY=-75.3 StartZ=0 EndX=-1.8 EndY=1.8 EndZ=0
    g4: Circle CenterX=3.1665 CenterY=-3.6665 CenterZ=0 NormalX=0 NormalY=0 NormalZ=1 AngleXU=0 Radius=1.7
    g5: Circle CenterX=3.1665 CenterY=-69.8335 CenterZ=0 NormalX=0 NormalY=0 NormalZ=1 AngleXU=0 Radius=1.7
    g6: Circle CenterX=118.284 CenterY=-69.8335 CenterZ=0 NormalX=0 NormalY=0 NormalZ=1 AngleXU=0 Radius=1.7
    g7: Circle CenterX=118.284 CenterY=-3.6665 CenterZ=0 NormalX=0 NormalY=0 NormalZ=1 AngleXU=0 Radius=1.7
    g8: LineSegment StartX=14.5 StartY=-19.5 StartZ=0 EndX=24.5 EndY=-19.5 EndZ=0
    g9: LineSegment StartX=24.5 StartY=-19.5 StartZ=0 EndX=24.5 EndY=-41 EndZ=0
    g10: LineSegment StartX=24.5 StartY=-41 StartZ=0 EndX=14.5 EndY=-41 EndZ=0
    g11: LineSegment StartX=14.5 StartY=-41 StartZ=0 EndX=14.5 EndY=-19.5 EndZ=0
    g12: Circle CenterX=125.725 CenterY=-55.875 CenterZ=0 NormalX=0 NormalY=0 NormalZ=1 AngleXU=0 Radius=5.5
  constraints (34):
    c: Coincident(g0,g1)
    c: Coincident(g1,g2)
    c: Coincident(g2,g3)
    c: Coincident(g3,g0)
    c: Horizontal(g0)
    c: Horizontal(g2)
    c: Vertical(g1)
    c: Vertical(g3)
    c: DistanceY(g0,g-4) = 0.2
    c: DistanceX(g-4,g0) = 0.2
    c: DistanceX(g1,g-3) = 0.2
    c: DistanceY(g-3,g1) = 0.2
    c: Coincident(g4,g-8)
    c: Coincident(g5,g-7)
    c: Coincident(g6,g-6)
    c: Coincident(g7,g-5)
    c: Radius(g7) = 1.7
    c: Equal(g7,g6)
    c: Equal(g6,g5)
    c: Equal(g5,g4)
    c: Coincident(g8,g9)
    c: Coincident(g9,g10)
    c: Coincident(g10,g11)
    c: Coincident(g11,g8)
    c: Horizontal(g8)
    c: Horizontal(g10)
    c: Vertical(g9)
    c: Vertical(g11)
    c: Coincident(g12,g-11)
    c: DistanceX(g-9,g9) = 0.5
    c: DistanceY(g9,g-9) = 0.5
    c: DistanceX(g8,g-10) = 0.5
    c: DistanceY(g-10,g8) = 0.5
    c: Radius(g12) = 5.5
FEATURE [PartDesign::Pad] Pad012
  Direction = (0,0,-1)
  Length = 2
  Length2 = 100
  Profile = -> Sketch021
  Reversed = true
  Type = 0
FEATURE [Sketcher::SketchObject] Sketch022
  ExternalGeometry = -> [Pad012]
  FullyConstrained = true
  MapMode = 5
  Placement = pos=(0,0,-6.7) rot=(0,0,1;0rad)
  Support = -> [Pad012]
  sketch-geometry (8):
    g0: Circle CenterX=118.284 CenterY=69.8335 CenterZ=0 NormalX=0 NormalY=0 NormalZ=1 AngleXU=0 Radius=4
    g1: Circle CenterX=118.284 CenterY=3.6665 CenterZ=0 NormalX=0 NormalY=0 NormalZ=1 AngleXU=0 Radius=4
    g2: Circle CenterX=3.1665 CenterY=3.6665 CenterZ=0 NormalX=0 NormalY=0 NormalZ=1 AngleXU=0 Radius=4
    g3: Circle CenterX=3.1665 CenterY=69.8335 CenterZ=0 NormalX=0 NormalY=0 NormalZ=1 AngleXU=0 Radius=4
    g4: Circle CenterX=3.1665 CenterY=69.8335 CenterZ=0 NormalX=0 NormalY=0 NormalZ=1 AngleXU=0 Radius=1.7
    g5: Circle CenterX=118.284 CenterY=69.8335 CenterZ=0 NormalX=0 NormalY=0 NormalZ=1 AngleXU=0 Radius=1.7
    g6: Circle CenterX=118.284 CenterY=3.6665 CenterZ=0 NormalX=0 NormalY=0 NormalZ=1 AngleXU=0 Radius=1.7
    g7: Circle CenterX=3.1665 CenterY=3.6665 CenterZ=0 NormalX=0 NormalY=0 NormalZ=1 AngleXU=0 Radius=1.7
  constraints (16):
    c: Coincident(g0,g-3)
    c: Coincident(g1,g-6)
    c: Coincident(g2,g-5)
    c: Coincident(g3,g-4)
    c: Radius(g0) = 4
    c: Equal(g1,g2)
    c: Equal(g2,g3)
    c: Equal(g1,g0)
    c: Coincident(g4,g3)
    c: Coincident(g5,g0)
    c: Coincident(g6,g1)
    c: Coincident(g7,g2)
    c: Equal(g4,g-4)
    c: Equal(g-3,g5)
    c: Equal(g6,g-6)
    c: Equal(g7,g-5)
FEATURE [PartDesign::Pad] Pad013
  BaseFeature = -> Pad012
  Direction = (0,0,1)
  Length = 10
  Length2 = 100
  Profile = -> Sketch022
  Type = 3
  UpToFace = -> Binder002 [Face4]
FEATURE [Sketcher::SketchObject] Sketch023
  ExternalGeometry = -> [Pad013]
  FullyConstrained = true
  MapMode = 5
  Placement = pos=(0,0,-8.7) rot=(1,0,0;3.14159rad)
  Support = -> [Pad013]
  sketch-geometry (4):
    g0: Circle CenterX=118.284 CenterY=-3.6665 CenterZ=0 NormalX=0 NormalY=0 NormalZ=1 AngleXU=0 Radius=3
    g1: Circle CenterX=3.1665 CenterY=-3.6665 CenterZ=0 NormalX=0 NormalY=0 NormalZ=1 AngleXU=0 Radius=3
    g2: Circle CenterX=3.1665 CenterY=-69.8335 CenterZ=0 NormalX=0 NormalY=0 NormalZ=1 AngleXU=0 Radius=3
    g3: Circle CenterX=118.284 CenterY=-69.8335 CenterZ=0 NormalX=0 NormalY=0 NormalZ=1 AngleXU=0 Radius=3
  constraints (8):
    c: Coincident(g0,g-3)
    c: Coincident(g1,g-6)
    c: Coincident(g2,g-5)
    c: Coincident(g3,g-4)
    c: Radius(g3) = 3
    c: Equal(g3,g0)
    c: Equal(g0,g1)
    c: Equal(g1,g2)
FEATURE [PartDesign::Pocket] Pocket005
  BaseFeature = -> Pad013
  Length = 4
  Length2 = 100
  Profile = -> Sketch023
  Type = 0
FEATURE [Sketcher::SketchObject] Sketch024
  ExternalGeometry = -> [Pocket005]
  FullyConstrained = true
  MapMode = 5
  Placement = pos=(0,0,-4.7) rot=(1,0,0;3.14159rad)
  Support = -> [Pocket005]
  sketch-geometry (4):
    g0: Circle CenterX=3.1665 CenterY=-3.6665 CenterZ=0 NormalX=0 NormalY=0 NormalZ=1 AngleXU=0 Radius=1.7
    g1: Circle CenterX=3.1665 CenterY=-69.8335 CenterZ=0 NormalX=0 NormalY=0 NormalZ=1 AngleXU=0 Radius=1.7
    g2: Circle CenterX=118.284 CenterY=-3.6665 CenterZ=0 NormalX=0 NormalY=0 NormalZ=1 AngleXU=0 Radius=1.7
    g3: Circle CenterX=118.284 CenterY=-69.8335 CenterZ=0 NormalX=0 NormalY=0 NormalZ=1 AngleXU=0 Radius=1.7
  constraints (8):
    c: Coincident(g0,g-5)
    c: Equal(g0,g-5)
    c: Coincident(g1,g-6)
    c: Equal(g1,g-6)
    c: Coincident(g2,g-4)
    c: Equal(g2,g-4)
    c: Coincident(g3,g-3)
    c: Equal(g3,g-3)
FEATURE [PartDesign::Pad] Pad014
  BaseFeature = -> Pocket005
  Direction = (0,0,-1)
  Length = 0.2
  Length2 = 100
  Profile = -> Sketch024
  Reversed = true
  Type = 0
FEATURE [Sketcher::SketchObject] Sketch025
  ExternalGeometry = -> [Pad014]
  FullyConstrained = true
  MapMode = 5
  Placement = pos=(0,0,-8.7) rot=(1,0,0;3.14159rad)
  Support = -> [Pad014]
  sketch-geometry (10):
    g0: Circle CenterX=33.2 CenterY=-60.3 CenterZ=0 NormalX=0 NormalY=0 NormalZ=1 AngleXU=0 Radius=1.375
    g1: Circle CenterX=107.8 CenterY=-60.3 CenterZ=0 NormalX=0 NormalY=0 NormalZ=1 AngleXU=0 Radius=1.375
    g2: Circle CenterX=70.5 CenterY=-13.2 CenterZ=0 NormalX=0 NormalY=0 NormalZ=1 AngleXU=0 Radius=1.375
    g3: LineSegment StartX=70.5 StartY=-13.2 StartZ=0 EndX=-1.8 EndY=-13.2 EndZ=0
    g4: LineSegment StartX=70.5 StartY=-13.2 StartZ=0 EndX=142.8 EndY=-13.2 EndZ=0
    g5: LineSegment StartX=70.5 StartY=-13.2 StartZ=0 EndX=70.5 EndY=1.8 EndZ=0
    g6: LineSegment StartX=33.2 StartY=-60.3 StartZ=0 EndX=107.8 EndY=-60.3 EndZ=0
    g7: LineSegment StartX=33.2 StartY=-60.3 StartZ=0 EndX=-1.8 EndY=-60.3 EndZ=0
    g8: LineSegment StartX=107.8 StartY=-60.3 StartZ=0 EndX=142.8 EndY=-60.3 EndZ=0
    g9: LineSegment StartX=33.2 StartY=-60.3 StartZ=0 EndX=33.2 EndY=-75.3 EndZ=0
  constraints (29):
    c: Coincident(g3,g2)
    c: PointOnObject(g3,g-3)
    c: Horizontal(g3)
    c: Coincident(g4,g2)
    c: PointOnObject(g4,g-4)
    c: Horizontal(g4)
    c: Coincident(g5,g2)
    c: PointOnObject(g5,g-5)
    c: Vertical(g5)
    c: Equal(g4,g3)
    c: Coincident(g6,g0)
    c: Coincident(g6,g1)
    c: Horizontal(g6)
    c: Coincident(g7,g0)
    c: PointOnObject(g7,g-3)
    c: Horizontal(g7)
    c: Coincident(g8,g1)
    c: PointOnObject(g8,g-4)
    c: Horizontal(g8)
    c: Equal(g8,g7)
    c: Radius(g2) = 1.375
    c: Equal(g2,g0)
    c: Equal(g0,g1)
    c: Distance(g5) = 15
    c: Coincident(g9,g0)
    c: PointOnObject(g9,g-6)
    c: Vertical(g9)
    c: Equal(g9,g5)
    c: Distance(g7) = 35
FEATURE [PartDesign::Pocket] Pocket006
  BaseFeature = -> Pad014
  Length = 5
  Length2 = 100
  Profile = -> Sketch025
  Type = 1
FEATURE [Sketcher::SketchObject] Sketch026
  ExternalGeometry = -> [Pocket006]
  FullyConstrained = true
  MapMode = 5
  Placement = pos=(0,0,-6.7) rot=(0,0,1;0rad)
  Support = -> [Pocket006]
  sketch-geometry (26):
    g0: LineSegment StartX=-1.8 StartY=75.3 StartZ=0 EndX=142.8 EndY=75.3 EndZ=0
    g1: LineSegment StartX=142.8 StartY=75.3 StartZ=0 EndX=142.8 EndY=-1.8 EndZ=0
    g2: LineSegment StartX=142.8 StartY=-1.8 StartZ=0 EndX=-1.8 EndY=-1.8 EndZ=0
    g3: LineSegment StartX=-1.8 StartY=-1.8 StartZ=0 EndX=-1.8 EndY=75.3 EndZ=0
    g4: LineSegment StartX=140.8 StartY=73.3 StartZ=0 EndX=140.8 EndY=0.2 EndZ=0
    g5: ArcOfCircle CenterX=3.1665 CenterY=3.6665 CenterZ=0 NormalX=0 NormalY=0 NormalZ=1 AngleXU=0 Radius=4 StartAngle=2.40629 EndAngle=5.23479
    g6: LineSegment StartX=0.2 StartY=6.34976 StartZ=0 EndX=0.2 EndY=67.1502 EndZ=0
    g7: LineSegment StartX=140.8 StartY=0.2 StartZ=0 EndX=78 EndY=0.2 EndZ=0
    g8: ArcOfCircle CenterX=3.1665 CenterY=69.8335 CenterZ=0 NormalX=0 NormalY=0 NormalZ=1 AngleXU=0 Radius=4 StartAngle=1.0484 EndAngle=3.8769
    g9: LineSegment StartX=5.16234 StartY=73.3 StartZ=0 EndX=111.418 EndY=73.3 EndZ=0
    g10: LineSegment StartX=14.5817 StartY=73.3 StartZ=0 EndX=63 EndY=10.2 EndZ=0
    g11: LineSegment StartX=29.5817 StartY=73.3 StartZ=0 EndX=70.5 EndY=19.9742 EndZ=0
    g12: LineSegment StartX=70.5 StartY=19.9742 StartZ=0 EndX=111.418 EndY=73.3 EndZ=0
    g13: LineSegment StartX=126.418 StartY=73.3 StartZ=0 EndX=78 EndY=10.2 EndZ=0
    g14: LineSegment StartX=70.5 StartY=19.9742 StartZ=0 EndX=70.5 EndY=0.2 EndZ=0
    g15: LineSegment StartX=126.418 StartY=73.3 StartZ=0 EndX=140.8 EndY=73.3 EndZ=0
    g16: LineSegment StartX=111.418 StartY=73.3 StartZ=0 EndX=126.418 EndY=73.3 EndZ=0
    g17: Circle CenterX=118.284 CenterY=69.8335 CenterZ=0 NormalX=0 NormalY=0 NormalZ=1 AngleXU=0 Radius=4
    g18: Circle CenterX=33.2 CenterY=60.3 CenterZ=0 NormalX=0 NormalY=0 NormalZ=1 AngleXU=0 Radius=1.375
    g19: Circle CenterX=107.8 CenterY=60.3 CenterZ=0 NormalX=0 NormalY=0 NormalZ=1 AngleXU=0 Radius=1.375
    g20: Circle CenterX=70.5 CenterY=13.2 CenterZ=0 NormalX=0 NormalY=0 NormalZ=1 AngleXU=0 Radius=1.375
    g21: LineSegment StartX=78 StartY=10.2 StartZ=0 EndX=78 EndY=0.2 EndZ=0
    g22: LineSegment StartX=63 StartY=10.2 StartZ=0 EndX=63 EndY=0.2 EndZ=0
    g23: LineSegment StartX=63 StartY=0.2 StartZ=0 EndX=5.16234 EndY=0.2 EndZ=0
    g24: LineSegment StartX=78 StartY=0.2 StartZ=0 EndX=70.5 EndY=0.2 EndZ=0
    g25: LineSegment StartX=70.5 StartY=0.2 StartZ=0 EndX=63 EndY=0.2 EndZ=0
  constraints (70):
    c: Coincident(g0,g1)
    c: Coincident(g1,g2)
    c: Coincident(g2,g3)
    c: Coincident(g3,g0)
    c: Horizontal(g0)
    c: Horizontal(g2)
    c: Vertical(g1)
    c: Vertical(g3)
    c: Coincident(g1,g-3)
    c: Coincident(g15,g4)
    c: Coincident(g4,g7)
    c: Vertical(g4)
    c: DistanceX(g4,g1) = 2
    c: DistanceY(g1,g4) = 2
    c: Coincident(g0,g-4)
    c: Coincident(g5,g-6)
    c: Equal(g5,g-6)
    c: Vertical(g6)
    c: Coincident(g6,g5)
    c: Horizontal(g7)
    c: Coincident(g23,g5)
    c: Coincident(g8,g-5)
    c: Coincident(g8,g6)
    c: Equal(g8,g-5)
    c: Horizontal(g9)
    c: Coincident(g9,g8)
    c: DistanceY(g8,g0) = 2
    c: DistanceX(g0,g6) = 2
    c: PointOnObject(g10,g9)
    c: PointOnObject(g11,g9)
    c: Coincident(g12,g11)
    c: Angle(g13,g10) = 1.309
    c: Parallel(g12,g13)
    c: Parallel(g11,g10)
    c: Coincident(g14,g11)
    c: Vertical(g14)
    c: PointOnObject(g-10,g14)
    c: DistanceX(g10,g11) = 15
    c: Coincident(g9,g12)
    c: Coincident(g16,g9)
    c: Coincident(g16,g13)
    c: Coincident(g13,g15)
    c: DistanceY(g4,g0) = 2
    c: Horizontal(g15)
    c: Coincident(g17,g-8)
    c: Equal(g17,g-8)
    c: Coincident(g18,g-11)
    c: Equal(g18,g-11)
    c: Coincident(g19,g-9)
    c: Equal(g19,g-9)
    c: Coincident(g20,g-10)
    c: Equal(g20,g-10)
    c: Vertical(g21)
    c: PointOnObject(g22,g7)
    c: Vertical(g22)
    c: Equal(g21,g22)
    c: DistanceX(g22,g21) = 15
    c: Coincident(g13,g21)
    c: Coincident(g10,g22)
    c: Coincident(g7,g21)
    c: Coincident(g24,g7)
    c: Coincident(g24,g14)
    c: Horizontal(g24)
    c: Coincident(g25,g14)
    c: Coincident(g25,g22)
    c: Equal(g25,g24)
    c: Distance(g21) = 10
    c: Equal(g11,g12)
    c: Coincident(g22,g23)
    c: Horizontal(g23)
FEATURE [PartDesign::Pad] Pad015
  BaseFeature = -> Pocket006
  Direction = (0,0,1)
  Length = 3
  Length2 = 100
  Profile = -> Sketch026
  Type = 0
FEATURE [PartDesign::SubShapeBinder] Binder003
  BindMode = 0
  ClaimChildren = false
  Context = -> Part [Body003.Binder003.]
  Fuse = false
  MakeFace = true
  PartialLoad = false
  Relative = true
  Support = -> [Body002]
  _Version = 2
FEATURE [Sketcher::SketchObject] Sketch027
  ExternalGeometry = -> [Binder003]
  FullyConstrained = true
  MapMode = 5
  Placement = pos=(0,0,-8.7) rot=(1,0,0;3.14159rad)
  Support = -> [Binder003]
  sketch-geometry (9):
    g0: LineSegment StartX=63 StartY=-0.2 StartZ=0 EndX=63 EndY=-10.2 EndZ=0
    g1: LineSegment StartX=63 StartY=-10.2 StartZ=0 EndX=14.5817 EndY=-73.3 EndZ=0
    g2: LineSegment StartX=14.5817 StartY=-73.3 StartZ=0 EndX=126.418 EndY=-73.3 EndZ=0
    g3: Circle CenterX=70.5 CenterY=-13.2 CenterZ=0 NormalX=0 NormalY=0 NormalZ=1 AngleXU=0 Radius=1.7
    g4: Circle CenterX=107.8 CenterY=-60.3 CenterZ=0 NormalX=0 NormalY=0 NormalZ=1 AngleXU=0 Radius=1.7
    g5: Circle CenterX=33.2 CenterY=-60.3 CenterZ=0 NormalX=0 NormalY=0 NormalZ=1 AngleXU=0 Radius=1.7
    g6: LineSegment StartX=63 StartY=-0.2 StartZ=0 EndX=102.8 EndY=-0.2 EndZ=0
    g7: LineSegment StartX=102.8 StartY=-0.2 StartZ=0 EndX=102.8 EndY=-42.52 EndZ=0
    g8: LineSegment StartX=102.8 StartY=-42.52 StartZ=0 EndX=126.418 EndY=-73.3 EndZ=0
  constraints (20):
    c: Coincident(g8,g2)
    c: Coincident(g-10,g2)
    c: PointOnObject(g8,g-10)
    c: Coincident(g7,g8)
    c: PointOnObject(g7,g-8)
    c: Vertical(g7)
    c: DistanceX(g7,g-9) = 40
    c: Coincident(g6,g7)
    c: Coincident(g1,g2)
    c: Coincident(g1,g-12)
    c: Coincident(g0,g1)
    c: Coincident(g0,g-7)
    c: Coincident(g0,g6)
    c: Coincident(g0,g-8)
    c: Coincident(g4,g-3)
    c: Coincident(g3,g-6)
    c: Radius(g3) = 1.7
    c: Equal(g4,g3)
    c: Equal(g5,g3)
    c: Coincident(g5,g-5)
FEATURE [PartDesign::Pad] Pad016
  Direction = (0,0,-1)
  Length = 3
  Length2 = 100
  Profile = -> Sketch027
  Type = 0
FEATURE [Sketcher::SketchObject] Sketch028
  ExternalGeometry = -> [Pad016]
  FullyConstrained = true
  MapMode = 5
  Placement = pos=(102.8,0,0) rot=(0.57735,0.57735,0.57735;2.0944rad)
  Support = -> [Pad016]
  sketch-geometry (5):
    g0: LineSegment StartX=0.2 StartY=-11.7 StartZ=0 EndX=48.475 EndY=-95.3148 EndZ=0
    g1: LineSegment StartX=48.475 StartY=-95.3148 StartZ=0 EndX=83.116 EndY=-75.3148 EndZ=0
    g2: LineSegment StartX=73.3 StartY=-11.7 StartZ=0 EndX=53.116 EndY=-23.3532 EndZ=0
    g3: LineSegment StartX=83.116 StartY=-75.3148 StartZ=0 EndX=53.116 EndY=-23.3532 EndZ=0
    g4: LineSegment StartX=73.3 StartY=-11.7 StartZ=0 EndX=0.2 EndY=-11.7 EndZ=0
  constraints (13):
    c: Coincident(g0,g-3)
    c: Coincident(g1,g0)
    c: Distance(g1) = 40
    c: Perpendicular(g1,g0)
    c: Angle(g0,g-3) = 1.0472
    c: Coincident(g2,g-4)
    c: Distance(g2,g1) = 60
    c: Coincident(g3,g1)
    c: Coincident(g3,g2)
    c: Parallel(g3,g0)
    c: Perpendicular(g3,g2)
    c: Coincident(g4,g2)
    c: Coincident(g4,g0)
FEATURE [PartDesign::Pad] Pad017
  BaseFeature = -> Pad016
  Direction = (1,0,0)
  Length = 3
  Length2 = 100
  Profile = -> Sketch028
  Reversed = true
  Type = 0
FEATURE [Sketcher::SketchObject] Sketch029
  ExternalGeometry = -> [Pad017]
  FullyConstrained = true
  MapMode = 5
  Placement = pos=(99.8,0,0) rot=(0.57735,-0.57735,-0.57735;2.0944rad)
  Support = -> [Pad017]
  sketch-geometry (10):
    g0: LineSegment StartX=-53.116 StartY=-23.3532 StartZ=0 EndX=-18.475 EndY=-43.3532 EndZ=0
    g1: LineSegment StartX=-44.1665 StartY=-28.5202 StartZ=0 EndX=-74.1665 EndY=-80.4818 EndZ=0
    g2: LineSegment StartX=-26.846 StartY=-38.5202 StartZ=0 EndX=-56.846 EndY=-90.4818 EndZ=0
    g3: LineSegment StartX=-78.116 StartY=-66.6545 StartZ=0 EndX=-43.475 EndY=-86.6545 EndZ=0
    g4: LineSegment StartX=-68.116 StartY=-49.334 StartZ=0 EndX=-33.475 EndY=-69.334 EndZ=0
    g5: Circle CenterX=-51.846 CenterY=-81.8215 CenterZ=0 NormalX=0 NormalY=0 NormalZ=1 AngleXU=0 Radius=1.7
    g6: Circle CenterX=-41.846 CenterY=-64.501 CenterZ=0 NormalX=0 NormalY=0 NormalZ=1 AngleXU=0 Radius=1.7
    g7: Circle CenterX=-64.1665 CenterY=-63.1612 CenterZ=0 NormalX=0 NormalY=0 NormalZ=1 AngleXU=0 Radius=1.7
    g8: LineSegment StartX=-64.1665 StartY=-63.1612 StartZ=0 EndX=-51.846 EndY=-81.8215 EndZ=0
    g9: LineSegment StartX=-64.1665 StartY=-63.1612 StartZ=0 EndX=-41.846 EndY=-64.501 EndZ=0
  constraints (32):
    c: PointOnObject(g1,g0)
    c: PointOnObject(g2,g0)
    c: Distance(g2,g1) = 20
    c: Parallel(g2,g1)
    c: Parallel(g4,g3)
    c: Distance(g3,g4) = 20
    c: PointOnObject(g5,g3)
    c: PointOnObject(g6,g2)
    c: PointOnObject(g6,g4)
    c: PointOnObject(g5,g2)
    c: Radius(g5) = 1.7
    c: Equal(g6,g5)
    c: PointOnObject(g7,g1)
    c: Equal(g7,g5)
    c: Coincident(g8,g7)
    c: Coincident(g8,g5)
    c: Coincident(g9,g7)
    c: Coincident(g9,g6)
    c: Equal(g8,g9)
    c: PointOnObject(g0,g-3)
    c: PointOnObject(g4,g-3)
    c: PointOnObject(g3,g-3)
    c: PointOnObject(g2,g-6)
    c: PointOnObject(g1,g-6)
    c: PointOnObject(g3,g-5)
    c: PointOnObject(g4,g-5)
    c: Parallel(g1,g-5)
    c: Parallel(g3,g-6)
    c: Coincident(g-5,g0)
    c: Perpendicular(g-3,g0)
    c: Distance(g3,g-6) = 10
    c: Distance(g1,g-6) = 10.334
FEATURE [PartDesign::Pocket] Pocket007
  BaseFeature = -> Pad017
  Length = 5
  Length2 = 100
  Profile = -> Sketch029
  Type = 1
FEATURE [Sketcher::SketchObject] Sketch030
  ExternalGeometry = -> [Pocket007]
  FullyConstrained = true
  MapMode = 5
  Placement = pos=(99.8,0,0) rot=(0.57735,-0.57735,-0.57735;2.0944rad)
  Support = -> [Pocket007]
  sketch-geometry (15):
    g0: LineSegment StartX=-0.2 StartY=-11.7 StartZ=0 EndX=-48.475 EndY=-95.3148 EndZ=0
    g1: LineSegment StartX=-42.9239 StartY=-11.7 StartZ=0 EndX=-80.5179 EndY=-76.8148 EndZ=0
    g2: LineSegment StartX=-83.116 StartY=-75.3148 StartZ=0 EndX=-80.5179 EndY=-76.8148 EndZ=0
    g3: LineSegment StartX=-51.0731 StartY=-93.8148 StartZ=0 EndX=-3.6641 EndY=-11.7 EndZ=0
    g4: LineSegment StartX=-51.0731 StartY=-93.8148 StartZ=0 EndX=-48.475 EndY=-95.3148 EndZ=0
    g5: LineSegment StartX=-3.6641 StartY=-11.7 StartZ=0 EndX=-0.2 EndY=-11.7 EndZ=0
    g6: LineSegment StartX=-21.562 StartY=-11.7 StartZ=0 EndX=-64.4965 EndY=-86.0648 EndZ=0
    g7: LineSegment StartX=-25.0261 StartY=-11.7 StartZ=0 EndX=-67.0945 EndY=-84.5648 EndZ=0
    g8: LineSegment StartX=-67.0945 StartY=-84.5648 StartZ=0 EndX=-64.4965 EndY=-86.0648 EndZ=0
    g9: LineSegment StartX=-21.562 StartY=-11.7 StartZ=0 EndX=-25.0261 EndY=-11.7 EndZ=0
    g10: LineSegment StartX=-64.4965 StartY=-86.0648 StartZ=0 EndX=-51.0731 EndY=-93.8148 EndZ=0
    g11: LineSegment StartX=-67.0945 StartY=-84.5648 StartZ=0 EndX=-80.5179 EndY=-76.8148 EndZ=0
    g12: LineSegment StartX=-42.9239 StartY=-11.7 StartZ=0 EndX=-73.3 EndY=-11.7 EndZ=0
    g13: LineSegment StartX=-73.3 StartY=-11.7 StartZ=0 EndX=-53.116 EndY=-23.3532 EndZ=0
    g14: LineSegment StartX=-53.116 StartY=-23.3532 StartZ=0 EndX=-83.116 EndY=-75.3148 EndZ=0
  constraints (38):
    c: Coincident(g2,g1)
    c: Distance(g2) = 3
    c: Parallel(g3,g0)
    c: Coincident(g4,g3)
    c: Coincident(g4,g0)
    c: Distance(g4) = 3
    c: Coincident(g5,g3)
    c: Coincident(g5,g0)
    c: Parallel(g7,g6)
    c: Parallel(g6,g1)
    c: Coincident(g8,g7)
    c: Coincident(g8,g6)
    c: Distance(g8) = 3
    c: Coincident(g9,g6)
    c: Coincident(g9,g7)
    c: Coincident(g10,g6)
    c: Coincident(g10,g3)
    c: Coincident(g11,g7)
    c: Coincident(g11,g1)
    c: Equal(g11,g10)
    c: Coincident(g12,g13)
    c: Coincident(g14,g13)
    c: Coincident(g14,g2)
    c: Coincident(g12,g1)
    c: Parallel(g1,g14)
    c: Coincident(g2,g-7)
    c: PointOnObject(g1,g-7)
    c: PointOnObject(g7,g-7)
    c: PointOnObject(g6,g-7)
    c: Coincident(g-7,g0)
    c: PointOnObject(g3,g-7)
    c: Coincident(g0,g-3)
    c: PointOnObject(g3,g-8)
    c: PointOnObject(g6,g-8)
    c: PointOnObject(g7,g-8)
    c: PointOnObject(g1,g-8)
    c: Coincident(g12,g-6)
    c: Coincident(g13,g-6)
FEATURE [PartDesign::Pad] Pad018
  BaseFeature = -> Pocket007
  Direction = (-1,0,0)
  Length = 5
  Length2 = 100
  Profile = -> Sketch030
  Type = 0
FEATURE [Sketcher::SketchObject] Sketch031
  ExternalGeometry = -> [Pad018]
  FullyConstrained = true
  MapMode = 5
  Placement = pos=(0,0,-11.7) rot=(1,0,0;3.14159rad)
  Support = -> [Pad018]
  sketch-geometry (16):
    g0: LineSegment StartX=94.8 StartY=-3.6641 StartZ=0 EndX=66 EndY=-3.6641 EndZ=0
    g1: LineSegment StartX=66 StartY=-3.6641 StartZ=0 EndX=66 EndY=-11.2184 EndZ=0
    g2: LineSegment StartX=66 StartY=-11.2184 StartZ=0 EndX=20.6651 EndY=-70.3 EndZ=0
    g3: LineSegment StartX=94.8 StartY=-0.2 StartZ=0 EndX=63 EndY=-0.2 EndZ=0
    g4: LineSegment StartX=63 StartY=-0.2 StartZ=0 EndX=63 EndY=-10.2 EndZ=0
    g5: LineSegment StartX=63 StartY=-10.2 StartZ=0 EndX=14.5817 EndY=-73.3 EndZ=0
    g6: LineSegment StartX=14.5817 StartY=-73.3 StartZ=0 EndX=94.8 EndY=-73.3 EndZ=0
    g7: LineSegment StartX=20.6651 StartY=-70.3 StartZ=0 EndX=57.402 EndY=-70.3 EndZ=0
    g8: LineSegment StartX=94.8 StartY=-70.3 StartZ=0 EndX=94.8 EndY=-73.3 EndZ=0
    g9: LineSegment StartX=66 StartY=-11.2184 StartZ=0 EndX=63.6199 EndY=-9.39208 EndZ=0
    g10: LineSegment StartX=94.8 StartY=-21.562 StartZ=0 EndX=57.402 EndY=-70.3 EndZ=0
    g11: LineSegment StartX=94.8 StartY=-25.0261 StartZ=0 EndX=60.0601 EndY=-70.3 EndZ=0
    g12: LineSegment StartX=60.0601 StartY=-70.3 StartZ=0 EndX=94.8 EndY=-70.3 EndZ=0
    g13: LineSegment StartX=60.0601 StartY=-70.3 StartZ=0 EndX=57.402 EndY=-70.3 EndZ=0
    g14: LineSegment StartX=94.8 StartY=-25.0261 StartZ=0 EndX=94.8 EndY=-21.562 EndZ=0
    g15: LineSegment StartX=94.8 StartY=-3.6641 StartZ=0 EndX=94.8 EndY=-0.2 EndZ=0
  constraints (39):
    c: Horizontal(g0)
    c: Coincident(g1,g0)
    c: Vertical(g1)
    c: Coincident(g2,g1)
    c: Coincident(g4,g3)
    c: Coincident(g5,g4)
    c: Coincident(g6,g5)
    c: Coincident(g7,g2)
    c: Horizontal(g7)
    c: Coincident(g8,g12)
    c: Coincident(g8,g6)
    c: Distance(g8) = 3
    c: DistanceX(g3,g0) = 3
    c: Coincident(g9,g1)
    c: PointOnObject(g9,g5)
    c: Perpendicular(g2,g9)
    c: Distance(g9) = 3
    c: Parallel(g11,g10)
    c: Parallel(g10,g2)
    c: Coincident(g7,g10)
    c: Coincident(g12,g11)
    c: Horizontal(g12)
    c: Coincident(g13,g11)
    c: Coincident(g13,g7)
    c: Horizontal(g13)
    c: Coincident(g3,g-3)
    c: Coincident(g4,g-4)
    c: Coincident(g3,g-6)
    c: Coincident(g0,g-6)
    c: Coincident(g5,g-4)
    c: Coincident(g6,g-5)
    c: PointOnObject(g8,g-5)
    c: Coincident(g10,g-7)
    c: Coincident(g11,g-7)
    c: Coincident(g14,g11)
    c: Coincident(g14,g10)
    c: Coincident(g15,g0)
    c: Coincident(g15,g3)
    c: Parallel(g2,g5)
FEATURE [PartDesign::Pad] Pad019
  BaseFeature = -> Pad018
  Direction = (0,0,-1)
  Length = 4
  Length2 = 100
  Profile = -> Sketch031
  Type = 0
FEATURE [Sketcher::SketchObject] Sketch034
  ExternalGeometry = -> [Pad015]
  FullyConstrained = true
  MapMode = 5
  Placement = pos=(0,0,-3.7) rot=(0,0,1;0rad)
  Support = -> [Pad015]
  sketch-geometry (8):
    g0: Circle CenterX=33.625 CenterY=54.875 CenterZ=0 NormalX=0 NormalY=0 NormalZ=1 AngleXU=0 Radius=3.125
    g1: LineSegment StartX=33.625 StartY=54.875 StartZ=0 EndX=33.625 EndY=51.75 EndZ=0
    g2: LineSegment StartX=33.625 StartY=54.875 StartZ=0 EndX=30.5 EndY=54.875 EndZ=0
    g3: LineSegment StartX=24.7871 StartY=60 StartZ=0 EndX=39.7871 EndY=60 EndZ=0
    g4: LineSegment StartX=32.6522 StartY=49.75 StartZ=0 EndX=47.6522 EndY=49.75 EndZ=0
    g5: LineSegment StartX=33.625 StartY=54.875 StartZ=0 EndX=33.625 EndY=58 EndZ=0
    g6: LineSegment StartX=39.7871 StartY=60 StartZ=0 EndX=47.6522 EndY=49.75 EndZ=0
    g7: LineSegment StartX=24.7871 StartY=60 StartZ=0 EndX=32.6522 EndY=49.75 EndZ=0
  constraints (24):
    c: Radius(g0) = 3.125
    c: Coincident(g1,g0)
    c: PointOnObject(g1,g0)
    c: Vertical(g1)
    c: Coincident(g2,g0)
    c: PointOnObject(g2,g0)
    c: Horizontal(g2)
    c: DistanceY(g-4,g1) = 10.75
    c: DistanceX(g-4,g2) = 6
    c: PointOnObject(g3,g-5)
    c: PointOnObject(g3,g-6)
    c: Horizontal(g3)
    c: PointOnObject(g4,g-5)
    c: PointOnObject(g4,g-6)
    c: Horizontal(g4)
    c: DistanceY(g4,g1) = 2
    c: Coincident(g5,g0)
    c: PointOnObject(g5,g0)
    c: Vertical(g5)
    c: DistanceY(g5,g3) = 2
    c: Coincident(g6,g3)
    c: Coincident(g6,g4)
    c: Coincident(g7,g3)
    c: Coincident(g7,g4)
FEATURE [PartDesign::Pocket] Pocket010
  BaseFeature = -> Pad015
  Length = 0
  Length2 = 100
  Profile = -> Sketch034
  Type = 3
  UpToFace = -> Pad015 [Face55]
FEATURE [PartDesign::Body] Body002  label="Back"
  Group = -> [Binder001,Binder002,Sketch021,Pad012,Sketch022,Pad013,Sketch023,Pocket005,Sketch024,Pad014,Sketch025,Pocket006,Sketch026,Pad015,Sketch034,Pocket010]
  Origin = -> Origin002
  Tip = -> Pocket010
FEATURE [Sketcher::SketchObject] Sketch036
  ExternalGeometry = -> [Pad019]
  FullyConstrained = true
  MapMode = 5
  Placement = pos=(94.8,0,0) rot=(0.57735,0.57735,0.57735;2.0944rad)
  Support = -> [Pad019]
  sketch-geometry (6):
    g0: LineSegment StartX=2.5094 StartY=-15.7 StartZ=0 EndX=0.2 EndY=-15.7 EndZ=0
    g1: LineSegment StartX=0.2 StartY=-15.7 StartZ=0 EndX=0.2 EndY=-11.7 EndZ=0
    g2: LineSegment StartX=0.2 StartY=-11.7 StartZ=0 EndX=2.5094 EndY=-15.7 EndZ=0
    g3: LineSegment StartX=23.8714 StartY=-15.7 StartZ=0 EndX=21.562 EndY=-11.7 EndZ=0
    g4: LineSegment StartX=21.562 StartY=-11.7 StartZ=0 EndX=21.562 EndY=-15.7 EndZ=0
    g5: LineSegment StartX=21.562 StartY=-15.7 StartZ=0 EndX=23.8714 EndY=-15.7 EndZ=0
  constraints (12):
    c: Coincident(g0,g-3)
    c: Coincident(g0,g-4)
    c: Coincident(g1,g0)
    c: Coincident(g1,g-4)
    c: Coincident(g2,g1)
    c: Coincident(g2,g0)
    c: Coincident(g3,g-5)
    c: Coincident(g3,g-6)
    c: Coincident(g4,g3)
    c: Coincident(g4,g-6)
    c: Coincident(g5,g4)
    c: Coincident(g5,g3)
FEATURE [PartDesign::Pocket] Pocket011
  BaseFeature = -> Pad019
  Length = 0
  Length2 = 100
  Profile = -> Sketch036
  Type = 3
  UpToFace = -> Pad019 [Face9]
FEATURE [Sketcher::SketchObject] Sketch037
  ExternalGeometry = -> [Pocket011]
  FullyConstrained = true
  MapMode = 5
  Placement = pos=(94.8,-4.491e-13,0) rot=(0.57735,0.57735,0.57735;2.0944rad)
  Support = -> [Pocket011]
  sketch-geometry (3):
    g0: LineSegment StartX=73.3 StartY=-11.7 StartZ=0 EndX=73.3 EndY=-15.7 EndZ=0
    g1: LineSegment StartX=73.3 StartY=-15.7 StartZ=0 EndX=66.3718 EndY=-15.7 EndZ=0
    g2: LineSegment StartX=73.3 StartY=-11.7 StartZ=0 EndX=66.3718 EndY=-15.7 EndZ=0
  constraints (7):
    c: Coincident(g0,g-4)
    c: Coincident(g0,g-3)
    c: Coincident(g1,g0)
    c: PointOnObject(g1,g-4)
    c: Horizontal(g1)
    c: Coincident(g2,g0)
    c: Coincident(g2,g1)
FEATURE [PartDesign::Pocket] Pocket012
  BaseFeature = -> Pocket011
  Length = 5
  Length2 = 100
  Profile = -> Sketch037
  Type = 1
FEATURE [PartDesign::Body] Body003  label="Mount - Left"
  Group = -> [Binder003,Sketch027,Pad016,Sketch028,Pad017,Sketch029,Pocket007,Sketch030,Pad018,Sketch031,Pad019,Sketch036,Pocket011,Sketch037,Pocket012]
  Origin = -> Origin003
  Tip = -> Pocket012
FEATURE [Part::Feature] Body003001  label="Mount - Left001"
  shape: bbox 111.8 x 82.92 x 86.61 mm, 50 faces (baked)
FEATURE [Part::Mirroring] Part__Mirroring  label="Mount - Right"
  Base = (70.5,0,0)
  Normal = (1,0,0)
  Source = -> Body003001
FEATURE [PartDesign::SubShapeBinder] Binder004
  BindMode = 0
  ClaimChildren = false
  Context = -> Part [Body003002.Binder004.]
  Fuse = false
  MakeFace = true
  PartialLoad = false
  Relative = true
  Support = -> [Body002]
  _Version = 2
FEATURE [Sketcher::SketchObject] Sketch040
  ExternalGeometry = -> [Binder004]
  FullyConstrained = true
  MapMode = 5
  Placement = pos=(0,0,-8.7) rot=(1,0,0;3.14159rad)
  Support = -> [Binder004]
  sketch-geometry (9):
    g0: LineSegment StartX=63 StartY=-0.2 StartZ=0 EndX=63 EndY=-10.2 EndZ=0
    g1: LineSegment StartX=63 StartY=-10.2 StartZ=0 EndX=14.5817 EndY=-73.3 EndZ=0
    g2: LineSegment StartX=14.5817 StartY=-73.3 StartZ=0 EndX=126.418 EndY=-73.3 EndZ=0
    g3: Circle CenterX=70.5 CenterY=-13.2 CenterZ=0 NormalX=0 NormalY=0 NormalZ=1 AngleXU=0 Radius=1.7
    g4: Circle CenterX=107.8 CenterY=-60.3 CenterZ=0 NormalX=0 NormalY=0 NormalZ=1 AngleXU=0 Radius=1.7
    g5: Circle CenterX=33.2 CenterY=-60.3 CenterZ=0 NormalX=0 NormalY=0 NormalZ=1 AngleXU=0 Radius=1.7
    g6: LineSegment StartX=63 StartY=-0.2 StartZ=0 EndX=102.8 EndY=-0.2 EndZ=0
    g7: LineSegment StartX=102.8 StartY=-0.2 StartZ=0 EndX=102.8 EndY=-42.52 EndZ=0
    g8: LineSegment StartX=102.8 StartY=-42.52 StartZ=0 EndX=126.418 EndY=-73.3 EndZ=0
  constraints (20):
    c: Coincident(g8,g2)
    c: Coincident(g-10,g2)
    c: PointOnObject(g8,g-10)
    c: Coincident(g7,g8)
    c: PointOnObject(g7,g-8)
    c: Vertical(g7)
    c: DistanceX(g7,g-9) = 40
    c: Coincident(g6,g7)
    c: Coincident(g1,g2)
    c: Coincident(g1,g-12)
    c: Coincident(g0,g1)
    c: Coincident(g0,g-7)
    c: Coincident(g0,g6)
    c: Coincident(g0,g-8)
    c: Coincident(g4,g-3)
    c: Coincident(g3,g-6)
    c: Radius(g3) = 1.7
    c: Equal(g4,g3)
    c: Equal(g5,g3)
    c: Coincident(g5,g-5)
FEATURE [PartDesign::Pad] Pad021
  Direction = (0,0,-1)
  Length = 3
  Length2 = 100
  Profile = -> Sketch040
  Type = 0
FEATURE [Sketcher::SketchObject] Sketch042
  ExternalGeometry = -> [Pad021]
  FullyConstrained = true
  MapMode = 5
  Placement = pos=(102.8,0,0) rot=(0.57735,0.57735,0.57735;2.0944rad)
  Support = -> [Pad021]
  sketch-geometry (5):
    g0: LineSegment StartX=0.2 StartY=-11.7 StartZ=0 EndX=48.475 EndY=-95.3148 EndZ=0
    g1: LineSegment StartX=48.475 StartY=-95.3148 StartZ=0 EndX=83.116 EndY=-75.3148 EndZ=0
    g2: LineSegment StartX=73.3 StartY=-11.7 StartZ=0 EndX=53.116 EndY=-23.3532 EndZ=0
    g3: LineSegment StartX=83.116 StartY=-75.3148 StartZ=0 EndX=53.116 EndY=-23.3532 EndZ=0
    g4: LineSegment StartX=73.3 StartY=-11.7 StartZ=0 EndX=0.2 EndY=-11.7 EndZ=0
  constraints (13):
    c: Coincident(g0,g-3)
    c: Coincident(g1,g0)
    c: Distance(g1) = 40
    c: Perpendicular(g1,g0)
    c: Angle(g0,g-3) = 1.0472
    c: Coincident(g2,g-4)
    c: Distance(g2,g1) = 60
    c: Coincident(g3,g1)
    c: Coincident(g3,g2)
    c: Parallel(g3,g0)
    c: Perpendicular(g3,g2)
    c: Coincident(g4,g2)
    c: Coincident(g4,g0)
FEATURE [PartDesign::Pad] Pad022
  BaseFeature = -> Pad021
  Direction = (1,0,0)
  Length = 3
  Length2 = 100
  Profile = -> Sketch042
  Reversed = true
  Type = 0
FEATURE [Sketcher::SketchObject] Sketch041
  ExternalGeometry = -> [Pad022]
  FullyConstrained = true
  MapMode = 5
  Placement = pos=(99.8,0,0) rot=(-0.57735,0.57735,0.57735;4.18879rad)
  Support = -> [Pad022]
  sketch-geometry (10):
    g0: LineSegment StartX=-53.116 StartY=-23.3532 StartZ=0 EndX=-18.475 EndY=-43.3532 EndZ=0
    g1: LineSegment StartX=-44.1665 StartY=-28.5202 StartZ=0 EndX=-74.1665 EndY=-80.4818 EndZ=0
    g2: LineSegment StartX=-26.846 StartY=-38.5202 StartZ=0 EndX=-56.846 EndY=-90.4818 EndZ=0
    g3: LineSegment StartX=-78.116 StartY=-66.6545 StartZ=0 EndX=-43.475 EndY=-86.6545 EndZ=0
    g4: LineSegment StartX=-68.116 StartY=-49.334 StartZ=0 EndX=-33.475 EndY=-69.334 EndZ=0
    g5: Circle CenterX=-51.846 CenterY=-81.8215 CenterZ=0 NormalX=0 NormalY=0 NormalZ=1 AngleXU=0 Radius=2.2
    g6: Circle CenterX=-41.846 CenterY=-64.501 CenterZ=0 NormalX=0 NormalY=0 NormalZ=1 AngleXU=0 Radius=2.2
    g7: Circle CenterX=-64.1665 CenterY=-63.1612 CenterZ=0 NormalX=0 NormalY=0 NormalZ=1 AngleXU=0 Radius=2.2
    g8: LineSegment StartX=-64.1665 StartY=-63.1612 StartZ=0 EndX=-51.846 EndY=-81.8215 EndZ=0
    g9: LineSegment StartX=-64.1665 StartY=-63.1612 StartZ=0 EndX=-41.846 EndY=-64.501 EndZ=0
  constraints (32):
    c: PointOnObject(g1,g0)
    c: PointOnObject(g2,g0)
    c: Distance(g2,g1) = 20
    c: Parallel(g2,g1)
    c: Parallel(g4,g3)
    c: Distance(g3,g4) = 20
    c: PointOnObject(g5,g3)
    c: PointOnObject(g6,g2)
    c: PointOnObject(g6,g4)
    c: PointOnObject(g5,g2)
    c: Radius(g5) = 2.2
    c: Equal(g6,g5)
    c: PointOnObject(g7,g1)
    c: Equal(g7,g5)
    c: Coincident(g8,g7)
    c: Coincident(g8,g5)
    c: Coincident(g9,g7)
    c: Coincident(g9,g6)
    c: Equal(g8,g9)
    c: PointOnObject(g0,g-3)
    c: PointOnObject(g4,g-3)
    c: PointOnObject(g3,g-3)
    c: PointOnObject(g2,g-6)
    c: PointOnObject(g1,g-6)
    c: PointOnObject(g3,g-5)
    c: PointOnObject(g4,g-5)
    c: Parallel(g1,g-5)
    c: Parallel(g3,g-6)
    c: Coincident(g-5,g0)
    c: Perpendicular(g-3,g0)
    c: Distance(g3,g-6) = 10
    c: Distance(g1,g-6) = 10.334
FEATURE [PartDesign::Pocket] Pocket013
  BaseFeature = -> Pad022
  Length = 5
  Length2 = 100
  Profile = -> Sketch041
  Type = 1
FEATURE [Sketcher::SketchObject] Sketch043
  ExternalGeometry = -> [Pocket013]
  FullyConstrained = true
  MapMode = 5
  Placement = pos=(99.8,0,0) rot=(-0.57735,0.57735,0.57735;4.18879rad)
  Support = -> [Pocket013]
  sketch-geometry (15):
    g0: LineSegment StartX=-0.2 StartY=-11.7 StartZ=0 EndX=-48.475 EndY=-95.3148 EndZ=0
    g1: LineSegment StartX=-42.9239 StartY=-11.7 StartZ=0 EndX=-80.5179 EndY=-76.8148 EndZ=0
    g2: LineSegment StartX=-83.116 StartY=-75.3148 StartZ=0 EndX=-80.5179 EndY=-76.8148 EndZ=0
    g3: LineSegment StartX=-51.0731 StartY=-93.8148 StartZ=0 EndX=-3.6641 EndY=-11.7 EndZ=0
    g4: LineSegment StartX=-51.0731 StartY=-93.8148 StartZ=0 EndX=-48.475 EndY=-95.3148 EndZ=0
    g5: LineSegment StartX=-3.6641 StartY=-11.7 StartZ=0 EndX=-0.2 EndY=-11.7 EndZ=0
    g6: LineSegment StartX=-21.562 StartY=-11.7 StartZ=0 EndX=-64.4965 EndY=-86.0648 EndZ=0
    g7: LineSegment StartX=-25.0261 StartY=-11.7 StartZ=0 EndX=-67.0945 EndY=-84.5648 EndZ=0
    g8: LineSegment StartX=-67.0945 StartY=-84.5648 StartZ=0 EndX=-64.4965 EndY=-86.0648 EndZ=0
    g9: LineSegment StartX=-21.562 StartY=-11.7 StartZ=0 EndX=-25.0261 EndY=-11.7 EndZ=0
    g10: LineSegment StartX=-64.4965 StartY=-86.0648 StartZ=0 EndX=-51.0731 EndY=-93.8148 EndZ=0
    g11: LineSegment StartX=-67.0945 StartY=-84.5648 StartZ=0 EndX=-80.5179 EndY=-76.8148 EndZ=0
    g12: LineSegment StartX=-42.9239 StartY=-11.7 StartZ=0 EndX=-73.3 EndY=-11.7 EndZ=0
    g13: LineSegment StartX=-73.3 StartY=-11.7 StartZ=0 EndX=-53.116 EndY=-23.3532 EndZ=0
    g14: LineSegment StartX=-53.116 StartY=-23.3532 StartZ=0 EndX=-83.116 EndY=-75.3148 EndZ=0
  constraints (38):
    c: Coincident(g2,g1)
    c: Distance(g2) = 3
    c: Parallel(g3,g0)
    c: Coincident(g4,g3)
    c: Coincident(g4,g0)
    c: Distance(g4) = 3
    c: Coincident(g5,g3)
    c: Coincident(g5,g0)
    c: Parallel(g7,g6)
    c: Parallel(g6,g1)
    c: Coincident(g8,g7)
    c: Coincident(g8,g6)
    c: Distance(g8) = 3
    c: Coincident(g9,g6)
    c: Coincident(g9,g7)
    c: Coincident(g10,g6)
    c: Coincident(g10,g3)
    c: Coincident(g11,g7)
    c: Coincident(g11,g1)
    c: Equal(g11,g10)
    c: Coincident(g12,g13)
    c: Coincident(g14,g13)
    c: Coincident(g14,g2)
    c: Coincident(g12,g1)
    c: Parallel(g1,g14)
    c: Coincident(g2,g-7)
    c: PointOnObject(g1,g-7)
    c: PointOnObject(g7,g-7)
    c: PointOnObject(g6,g-7)
    c: Coincident(g-7,g0)
    c: PointOnObject(g3,g-7)
    c: Coincident(g0,g-3)
    c: PointOnObject(g3,g-8)
    c: PointOnObject(g6,g-8)
    c: PointOnObject(g7,g-8)
    c: PointOnObject(g1,g-8)
    c: Coincident(g12,g-6)
    c: Coincident(g13,g-6)
FEATURE [PartDesign::Pad] Pad020
  BaseFeature = -> Pocket013
  Direction = (-1,0,0)
  Length = 5
  Length2 = 100
  Profile = -> Sketch043
  Type = 0
FEATURE [Sketcher::SketchObject] Sketch038
  ExternalGeometry = -> [Pad020]
  FullyConstrained = true
  MapMode = 5
  Placement = pos=(0,0,-11.7) rot=(1,0,0;3.14159rad)
  Support = -> [Pad020]
  sketch-geometry (16):
    g0: LineSegment StartX=94.8 StartY=-3.6641 StartZ=0 EndX=66 EndY=-3.6641 EndZ=0
    g1: LineSegment StartX=66 StartY=-3.6641 StartZ=0 EndX=66 EndY=-11.2184 EndZ=0
    g2: LineSegment StartX=66 StartY=-11.2184 StartZ=0 EndX=20.6651 EndY=-70.3 EndZ=0
    g3: LineSegment StartX=94.8 StartY=-0.2 StartZ=0 EndX=63 EndY=-0.2 EndZ=0
    g4: LineSegment StartX=63 StartY=-0.2 StartZ=0 EndX=63 EndY=-10.2 EndZ=0
    g5: LineSegment StartX=63 StartY=-10.2 StartZ=0 EndX=14.5817 EndY=-73.3 EndZ=0
    g6: LineSegment StartX=14.5817 StartY=-73.3 StartZ=0 EndX=94.8 EndY=-73.3 EndZ=0
    g7: LineSegment StartX=20.6651 StartY=-70.3 StartZ=0 EndX=57.402 EndY=-70.3 EndZ=0
    g8: LineSegment StartX=94.8 StartY=-70.3 StartZ=0 EndX=94.8 EndY=-73.3 EndZ=0
    g9: LineSegment StartX=66 StartY=-11.2184 StartZ=0 EndX=63.6199 EndY=-9.39208 EndZ=0
    g10: LineSegment StartX=94.8 StartY=-21.562 StartZ=0 EndX=57.402 EndY=-70.3 EndZ=0
    g11: LineSegment StartX=94.8 StartY=-25.0261 StartZ=0 EndX=60.0601 EndY=-70.3 EndZ=0
    g12: LineSegment StartX=60.0601 StartY=-70.3 StartZ=0 EndX=94.8 EndY=-70.3 EndZ=0
    g13: LineSegment StartX=60.0601 StartY=-70.3 StartZ=0 EndX=57.402 EndY=-70.3 EndZ=0
    g14: LineSegment StartX=94.8 StartY=-25.0261 StartZ=0 EndX=94.8 EndY=-21.562 EndZ=0
    g15: LineSegment StartX=94.8 StartY=-3.6641 StartZ=0 EndX=94.8 EndY=-0.2 EndZ=0
  constraints (39):
    c: Horizontal(g0)
    c: Coincident(g1,g0)
    c: Vertical(g1)
    c: Coincident(g2,g1)
    c: Coincident(g4,g3)
    c: Coincident(g5,g4)
    c: Coincident(g6,g5)
    c: Coincident(g7,g2)
    c: Horizontal(g7)
    c: Coincident(g8,g12)
    c: Coincident(g8,g6)
    c: Distance(g8) = 3
    c: DistanceX(g3,g0) = 3
    c: Coincident(g9,g1)
    c: PointOnObject(g9,g5)
    c: Perpendicular(g2,g9)
    c: Distance(g9) = 3
    c: Parallel(g11,g10)
    c: Parallel(g10,g2)
    c: Coincident(g7,g10)
    c: Coincident(g12,g11)
    c: Horizontal(g12)
    c: Coincident(g13,g11)
    c: Coincident(g13,g7)
    c: Horizontal(g13)
    c: Coincident(g3,g-3)
    c: Coincident(g4,g-4)
    c: Coincident(g3,g-6)
    c: Coincident(g0,g-6)
    c: Coincident(g5,g-4)
    c: Coincident(g6,g-5)
    c: PointOnObject(g8,g-5)
    c: Coincident(g10,g-7)
    c: Coincident(g11,g-7)
    c: Coincident(g14,g11)
    c: Coincident(g14,g10)
    c: Coincident(g15,g0)
    c: Coincident(g15,g3)
    c: Parallel(g2,g5)
FEATURE [PartDesign::Pad] Pad023
  BaseFeature = -> Pad020
  Direction = (0,0,-1)
  Length = 4
  Length2 = 100
  Profile = -> Sketch038
  Type = 0
FEATURE [Sketcher::SketchObject] Sketch044
  ExternalGeometry = -> [Pad023]
  FullyConstrained = true
  MapMode = 5
  Placement = pos=(94.8,0,0) rot=(0.57735,0.57735,0.57735;2.0944rad)
  Support = -> [Pad023]
  sketch-geometry (6):
    g0: LineSegment StartX=2.5094 StartY=-15.7 StartZ=0 EndX=0.2 EndY=-15.7 EndZ=0
    g1: LineSegment StartX=0.2 StartY=-15.7 StartZ=0 EndX=0.2 EndY=-11.7 EndZ=0
    g2: LineSegment StartX=0.2 StartY=-11.7 StartZ=0 EndX=2.5094 EndY=-15.7 EndZ=0
    g3: LineSegment StartX=23.8714 StartY=-15.7 StartZ=0 EndX=21.562 EndY=-11.7 EndZ=0
    g4: LineSegment StartX=21.562 StartY=-11.7 StartZ=0 EndX=21.562 EndY=-15.7 EndZ=0
    g5: LineSegment StartX=21.562 StartY=-15.7 StartZ=0 EndX=23.8714 EndY=-15.7 EndZ=0
  constraints (12):
    c: Coincident(g0,g-3)
    c: Coincident(g0,g-4)
    c: Coincident(g1,g0)
    c: Coincident(g1,g-4)
    c: Coincident(g2,g1)
    c: Coincident(g2,g0)
    c: Coincident(g3,g-5)
    c: Coincident(g3,g-6)
    c: Coincident(g4,g3)
    c: Coincident(g4,g-6)
    c: Coincident(g5,g4)
    c: Coincident(g5,g3)
FEATURE [PartDesign::Pocket] Pocket015
  BaseFeature = -> Pad023
  Length = 0
  Length2 = 100
  Profile = -> Sketch044
  Type = 3
  UpToFace = -> Pad023 [Face9]
FEATURE [Sketcher::SketchObject] Sketch039
  ExternalGeometry = -> [Pocket015]
  FullyConstrained = true
  MapMode = 5
  Placement = pos=(94.8,-4.491e-13,0) rot=(0.57735,0.57735,0.57735;2.0944rad)
  Support = -> [Pocket015]
  sketch-geometry (3):
    g0: LineSegment StartX=73.3 StartY=-11.7 StartZ=0 EndX=73.3 EndY=-15.7 EndZ=0
    g1: LineSegment StartX=73.3 StartY=-15.7 StartZ=0 EndX=66.3718 EndY=-15.7 EndZ=0
    g2: LineSegment StartX=73.3 StartY=-11.7 StartZ=0 EndX=66.3718 EndY=-15.7 EndZ=0
  constraints (7):
    c: Coincident(g0,g-4)
    c: Coincident(g0,g-3)
    c: Coincident(g1,g0)
    c: PointOnObject(g1,g-4)
    c: Horizontal(g1)
    c: Coincident(g2,g0)
    c: Coincident(g2,g1)
FEATURE [PartDesign::Pocket] Pocket014
  BaseFeature = -> Pocket015
  Length = 5
  Length2 = 100
  Profile = -> Sketch039
  Type = 1
FEATURE [PartDesign::Body] Body003002  label="Mount - Left - Stock Screws"
  Group = -> [Binder004,Sketch040,Pad021,Sketch042,Pad022,Sketch041,Pocket013,Sketch043,Pad020,Sketch038,Pad023,Sketch044,Pocket015,Sketch039,Pocket014]
  Origin = -> Origin005
  Tip = -> Pocket014
FEATURE [Part::Feature] Body003002001  label="Mount - Left - Stock Screws001"
  shape: bbox 111.8 x 82.92 x 86.61 mm, 50 faces (baked)
FEATURE [Part::Mirroring] Part__Mirroring001  label="Mount - Right - Stock Screws"
  Base = (70.5,0,0)
  Normal = (1,0,0)
  Source = -> Body003002001
FEATURE [App::Part] Part
  Group = -> [Body002,Body001,Body,Body003,Body003001,Part__Mirroring,Body003002,Body003002001,Part__Mirroring001]
  Origin = -> Origin004
  Placement = pos=(0,0,0) rot=(-1,0,0;5.23599rad)
